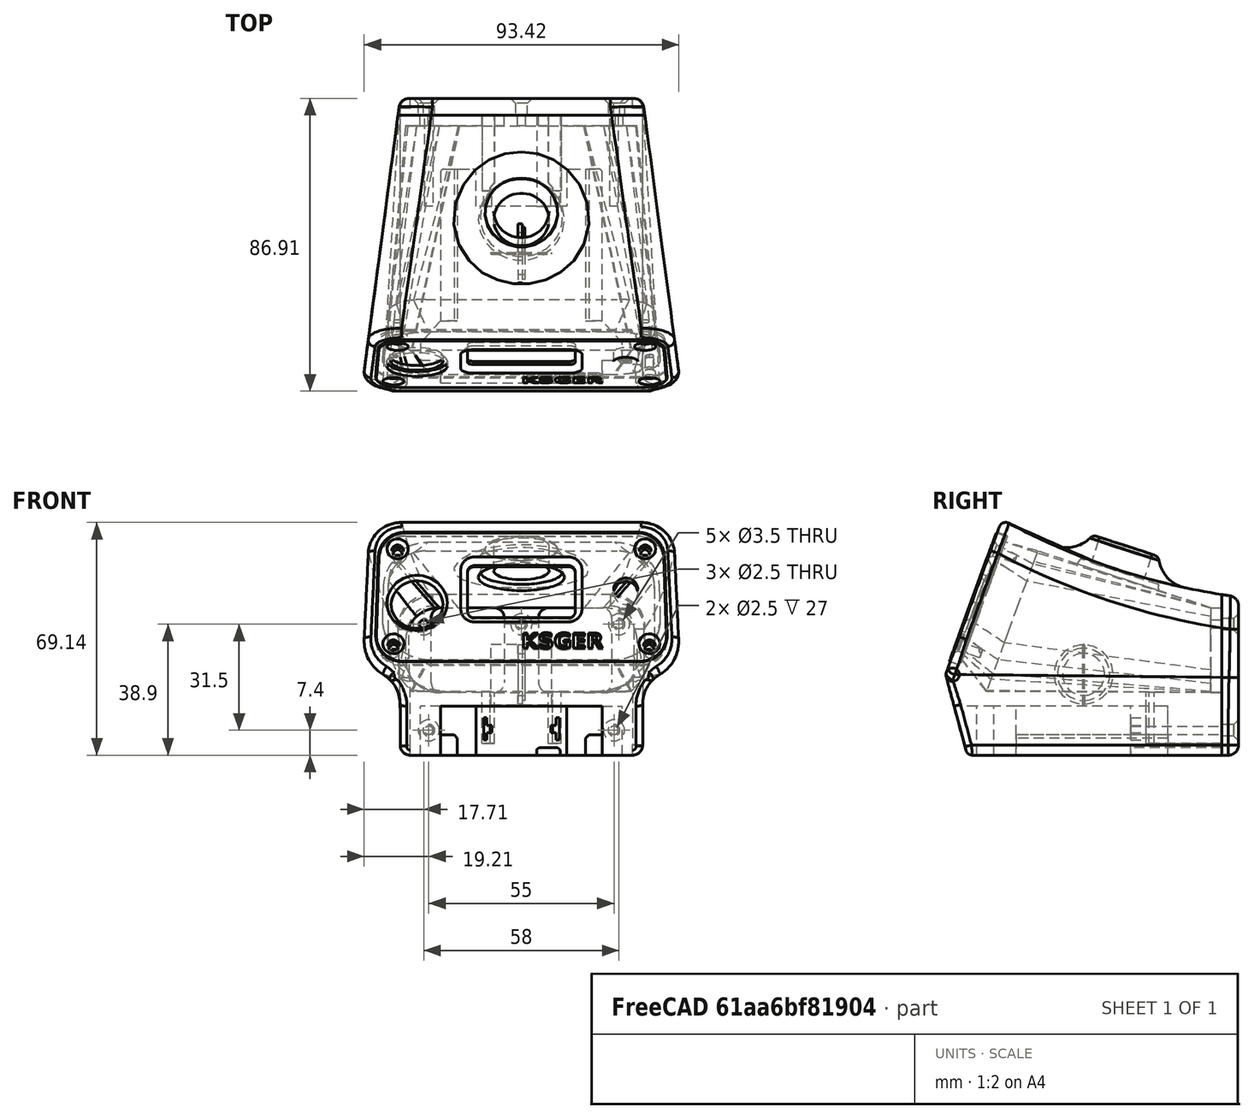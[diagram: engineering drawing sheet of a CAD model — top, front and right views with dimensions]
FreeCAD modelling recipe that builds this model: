
FCSTD DOCUMENT  (FreeCAD 2022.709R28846 (Git))
Label: solder_station5b_snap
License: All rights reserved
LicenseURL: http://en.wikipedia.org/wiki/All_rights_reserved
objects: Sketcher::SketchObject×22, PartDesign::Pocket×12, PartDesign::Fillet×8, Part::FeaturePython×6, Mesh::Feature×5, App::DocumentObjectGroup×4, PartDesign::Body×4, PartDesign::Chamfer×3, PartDesign::FeatureBase×2, PartDesign::Pad×2, PartDesign::Revolution×2, Spreadsheet::Sheet×1, Part::Plane×1, Part::Loft×1, Part::Extrusion×1, Part::MultiCommon×1, Part::Box×1, PartDesign::SubtractiveLoft×1, PartDesign::Groove×1, Part::Part2DObjectPython×1, +2 more types
note: 130 computed .brp shape members not serialized (recipe doc carries the construction recipe); baked Part::Feature solids carry a one-line shape summary decoded from their .brp

FEATURE [Sketcher::SketchObject] Sketch  label="RearSupport"
  ArcFitTolerance = 0
  AttachmentOffset = pos=(0,0,-37.8) rot=(0,0,1;0rad)
  AttachmentSupport = -> [XZ_Plane005]
  FullyConstrained = true
  MapMode = 5
  Placement = pos=(0,37.8,8.4e-15) rot=(1,0,0;1.5708rad)
  Support = -> [XZ_Plane005]
  TreeRank = 0
  expr: AttachmentOffset.Base.z = -<<param>>.mid_depth / 2 + <<param>>.wall
  expr: Constraints[24] = 3
  expr: Constraints[37] = <<param>>.bottom_height
  expr: Constraints[38] = <<param>>.floor
  expr: Constraints[39] = <<param>>.rear_height - <<param>>.wall
  expr: Constraints[47] = <<param>>.reart_screw_width2
  expr: Constraints[48] = <<param>>.rear_screw_width1
  expr: Constraints[49] = <<param>>.screw_hole
  expr: Constraints[50] = <<param>>.rear_screw_height
  expr: Constraints[51] = <<param>>.rear_screw_height
  expr: Constraints[52] = <<param>>.rear_screw_offset
  sketch-geometry (22):
    g0: LineSegment StartX=-23.8 StartY=19.8 StartZ=0 EndX=-8.1 EndY=19.8 EndZ=0
    g1: LineSegment StartX=26.8 StartY=16.8 StartZ=0 EndX=26.8 EndY=-2.4 EndZ=0
    g2: LineSegment StartX=23.8 StartY=-5.4 StartZ=0 EndX=8.1 EndY=-5.4 EndZ=0
    g3: LineSegment StartX=-26.8 StartY=-2.4 StartZ=0 EndX=-26.8 EndY=16.8 EndZ=0
    g4: LineSegment StartX=-5.1 StartY=16.8 StartZ=0 EndX=-5.1 EndY=-2.4 EndZ=0
    g5: LineSegment StartX=5.1 StartY=16.8 StartZ=0 EndX=5.1 EndY=-2.4 EndZ=0
    g6: LineSegment StartX=8.1 StartY=19.8 StartZ=0 EndX=23.8 EndY=19.8 EndZ=0
    g7: LineSegment StartX=-8.1 StartY=-5.4 StartZ=0 EndX=-23.8 EndY=-5.4 EndZ=0
    g8: ArcOfCircle CenterX=-8.1 CenterY=16.8 CenterZ=0 NormalX=0 NormalY=0 NormalZ=1 AngleXU=0 Radius=3 StartAngle=0 EndAngle=1.5708
    g9: ArcOfCircle CenterX=8.1 CenterY=16.8 CenterZ=0 NormalX=0 NormalY=0 NormalZ=1 AngleXU=0 Radius=3 StartAngle=1.5708 EndAngle=3.14159
    g10: ArcOfCircle CenterX=-8.1 CenterY=-2.4 CenterZ=0 NormalX=0 NormalY=0 NormalZ=1 AngleXU=0 Radius=3 StartAngle=4.71239 EndAngle=6.28319
    g11: ArcOfCircle CenterX=8.1 CenterY=-2.4 CenterZ=0 NormalX=0 NormalY=0 NormalZ=1 AngleXU=0 Radius=3 StartAngle=3.14159 EndAngle=4.71239
    g12: ArcOfCircle CenterX=-23.8 CenterY=16.8 CenterZ=0 NormalX=0 NormalY=0 NormalZ=1 AngleXU=0 Radius=3 StartAngle=1.5708 EndAngle=3.14159
    g13: ArcOfCircle CenterX=-23.8 CenterY=-2.4 CenterZ=0 NormalX=0 NormalY=0 NormalZ=1 AngleXU=0 Radius=3 StartAngle=3.14159 EndAngle=4.71239
    g14: ArcOfCircle CenterX=23.8 CenterY=16.8 CenterZ=0 NormalX=0 NormalY=0 NormalZ=1 AngleXU=0 Radius=3 StartAngle=3e-16 EndAngle=1.5708
    g15: ArcOfCircle CenterX=23.8 CenterY=-2.4 CenterZ=0 NormalX=0 NormalY=0 NormalZ=1 AngleXU=0 Radius=3 StartAngle=4.71239 EndAngle=6.28319
    g16: Circle [constr] CenterX=0 CenterY=-24 CenterZ=0 NormalX=0 NormalY=0 NormalZ=1 AngleXU=0 Radius=3
    g17: Circle CenterX=0 CenterY=14.9 CenterZ=0 NormalX=0 NormalY=0 NormalZ=1 AngleXU=0 Radius=1.25
    g18: Circle CenterX=-29 CenterY=14.9 CenterZ=0 NormalX=0 NormalY=0 NormalZ=1 AngleXU=0 Radius=1.25
    g19: Circle [constr] CenterX=-27.5 CenterY=-16.6 CenterZ=0 NormalX=0 NormalY=0 NormalZ=1 AngleXU=0 Radius=1.25
    g20: Circle [constr] CenterX=27.5 CenterY=-16.6 CenterZ=0 NormalX=0 NormalY=0 NormalZ=1 AngleXU=0 Radius=1.25
    g21: Circle CenterX=29 CenterY=14.9 CenterZ=0 NormalX=0 NormalY=0 NormalZ=1 AngleXU=0 Radius=1.25
  constraints (53):
    c: Horizontal(g0)
    c: Horizontal(g2)
    c: Vertical(g1)
    c: Vertical(g3)
    c: Vertical(g4)
    c: Vertical(g5)
    c: Tangent(g0,g6)
    c: Tangent(g2,g7)
    c: Tangent(g0,g8) = 1.5708
    c: Tangent(g4,g8) = 1.5708
    c: Tangent(g5,g9) = -1.5708
    c: Tangent(g6,g9) = 1.5708
    c: Tangent(g7,g10) = 1.5708
    c: Tangent(g4,g10) = 1.5708
    c: Tangent(g5,g11) = -1.5708
    c: Tangent(g2,g11) = 1.5708
    c: Tangent(g0,g12) = 1.5708
    c: Tangent(g3,g12) = 1.5708
    c: Tangent(g3,g13) = 1.5708
    c: Tangent(g7,g13) = 1.5708
    c: Tangent(g6,g14) = 1.5708
    c: Tangent(g1,g14) = 1.5708
    c: Tangent(g1,g15) = 1.5708
    c: Tangent(g2,g15) = 1.5708
    c: Radius(g9) = 3
    c: Equal(g12,g13)
    c: Equal(g13,g10)
    c: Equal(g10,g8)
    c: Equal(g11,g15)
    c: Equal(g15,g14)
    c: Equal(g14,g9)
    c: DistanceX(g4,g-1) = 5.1
    c: DistanceX(g5,g1) = 21.7
    c: Symmetric(g4,g5,g-2)
    c: Equal(g7,g2)
    c: PointOnObject(g16,g-2)
    c: Radius(g16) = 3
    c: DistanceY(g16,g-1) = 24
    c: DistanceY(g16,g2) = 18.6
    c: DistanceY(g16,g6) = 43.8
    c: PointOnObject(g17,g-2)
    c: Equal(g21,g18)
    c: Equal(g18,g19)
    c: Equal(g19,g20)
    c: Equal(g18,g17)
    c: Symmetric(g20,g19,g-2)
    c: Symmetric(g18,g21,g-2)
    c: DistanceX(g19,g20) = 55
    c: DistanceX(g18,g21) = 58
    c: Diameter(g19) = 2.5
    c: DistanceY(g20,g21) = 31.5
    c: DistanceY(g20,g17) = 31.5
    c: DistanceY(g16,g19) = 7.4
FEATURE [Spreadsheet::Sheet] Spreadsheet  label="param"
  PythonMode = false
  ShowCells = 0
  TreeRank = 0
  cells = A1=Body; B2=top_depth; C2(top_depth)=70; B3=mid_depth; C3(mid_depth)=82; D3=half is rear reference; B4=bottom_depth; C4(bottom_depth)=75; B6=bottom_width; C6(bottom_width)=72; B7=bottom_height; C7(bottom_height)=24; B8=bottom_angle; C8(bottom_angle)=15; B10=rear_width; C10(rear_width)=72; B11=rear_height; C11(rear_height)=47; F11=41; B13=mid_width; C13(mid_width)=80; B14=mid_height; C14(mid_height)=56; F14=50; B16=front_width1; C16(front_width1)=92; D16=@top; E16=upper; F16=91; B17=front_width2; C17(front_width2)=95; D17=@mid; E17=lower; F17=94; B18=front_height; C18(front_height)=70; F18=64; B19=front_angle; C19(front_angle)=20; B21=wall; C21(wall)=3.2; B22=radius_big; C22(radius_big)=10; B23=radius_medium; C23(radius_medium)=3; B24=radius_small; C24(radius_small)=2; B25=arch; C25(arch)=200; A27=Button; B28=button_offset; C28(button_offset)=10; B29=button_inside_dia; C29(button_inside_dia)=20; B30=button_outside_dia; C30(button_outside_dia)=22; B31=button_height; C31(button_height)=30.6; F31=26; B32=button_extension; C32(button_extension)=8; B33=button_fillet; C33(button_fillet)=12; B34=button_angle; C34(button_angle)=-18; F34=-17; B35=button_hole; C35(button_hole)=16.4; B36=button_hole_center; C36(button_hole_center)=-0.5; A38=Battery Cuts; B39=batt_carveout; C39(batt_carveout)=14.6; B40=batt_rail; C40(batt_rail)=6; B41=batt_rail_length; C41(batt_rail_length)=45; A43=Terminals; B44=terminal_height; C44(terminal_height)=6.6; B45=terminal_thickness; C45(terminal_thickness)=1; B46=terminal_seperation; C46(terminal_seperation)=21.5; B47=terminal_offset; C47(terminal_offset)=4.5; B48=terminal_depth; C48(terminal_depth)=22.5; A50=Box Interior; B51=floor; C51(floor)=18.6; B52=rear_inside_width; C52(rear_inside_width)==C10 - C21; D52=calc; B53=rear_inside_height; C53(rear_inside_height)==C11 - C21; D53=calc; B54=mid_inside_width; C54(mid_inside_width)==C13; D54=calc; B55=mid_inside_height; C55(mid_inside_height)==C14 + 7; D55=calc; F55=6; B56=front_inside_width1; C56(front_inside_width1)==C63 - C59 * 2; D56=calc; E56=upper; B57=front_inside_width2; C57(front_inside_width2)==C64 - C59 * 2; D57=calc; E57=lower; B58=front_inside_height; C58(front_inside_height)==C65 - C60 * 2; D58=calc; B59=front_width_lip_width; C59(front_width_lip_width)=3; B60=front_inside_lip_height; C60(front_inside_lip_height)=2; A62=Face; B63=face_width1; C63(face_width1)==84 + 1; B64=face_width2; C64(face_width2)==85.5 + 1; B65=face_height; C65(face_height)=41; F65=35; B66=face_thickness; C66(face_thickness)=3; B67=face_radius; C67(face_radius)=8; B68=face_offset; C68(face_offset)=2.8; F68=2.8; A70=Screws; B71=screw_hole; C71(screw_hole)=2.5; B73=front_screw_width1; C73(front_screw_width1)=73.5; D73=upper; B74=front_screw_width2; C74(front_screw_width2)=76; D74=lower; B75=front_screw_height; C75(front_screw_height)=30; F75=24; B76=front_screw_offset; C76(front_screw_offset)=5.5; B78=rear_screw_width1; C78(rear_screw_width1)=58; B79=reart_screw_width2; C79(reart_screw_width2)=55; B80=rear_screw_height; C80(rear_screw_height)=31.5; F80=25.5; B81=rear_screw_offset; C81(rear_screw_offset)=7.4; A83=Back; B84=back_thickness; C84(back_thickness)=5
FEATURE [Sketcher::SketchObject] Sketch008  label="SketchButtonHole"
  ArcFitTolerance = 0
  AttachmentOffset = pos=(0,-0.5,30.6) rot=(1,0,0;-0.314159rad)
  AttachmentSupport = -> [XY_Plane005]
  FullyConstrained = true
  MapMode = 5
  Placement = pos=(0,-0.5,30.6) rot=(1,0,0;5.96903rad)
  Support = -> [XY_Plane005]
  TreeRank = 0
  expr: AttachmentOffset.Base.y = <<param>>.button_hole_center
  expr: AttachmentOffset.Base.z = <<param>>.button_height
  expr: AttachmentOffset.Rotation.Angle = <<param>>.button_angle
  expr: Constraints[0] = <<param>>.button_hole
  expr: Constraints[2] = <<param>>.button_offset
  sketch-geometry (1):
    g0: Circle CenterX=0 CenterY=10 CenterZ=0 NormalX=0 NormalY=0 NormalZ=1 AngleXU=0 Radius=8.2
  constraints (3):
    c: Diameter(g0) = 16.4
    c: PointOnObject(g0,g-2)
    c: DistanceY(g-1,g0) = 10
FEATURE [Sketcher::SketchObject] Sketch012  label="SketchSide"
  ArcFitTolerance = 0
  AttachmentOffset = pos=(2.5,0,0) rot=(0,0,1;0rad)
  AttachmentSupport = -> [YZ_Plane006]
  FullyConstrained = true
  MapMode = 5
  Placement = pos=(6e-16,2.5,-6e-16) rot=(0.57735,0.57735,0.57735;2.0944rad)
  Support = -> [YZ_Plane006]
  TreeRank = 0
  expr: AttachmentOffset.Base.x = <<param>>.back_thickness / 2
  expr: Constraints[10] = <<param>>.bottom_height
  expr: Constraints[11] = 90 - <<param>>.bottom_angle
  expr: Constraints[12] = 90 - <<param>>.front_angle
  expr: Constraints[16] = <<param>>.front_height
  expr: Constraints[4] = <<param>>.rear_height - <<param>>.bottom_height
  expr: Constraints[5] = <<param>>.arch
  expr: Constraints[6] = <<param>>.mid_depth + <<param>>.back_thickness
  sketch-geometry (6):
    g0: LineSegment StartX=43.5 StartY=0 StartZ=0 EndX=43.5 EndY=23 EndZ=0
    g1: LineSegment StartX=-43.5 StartY=0 StartZ=0 EndX=-26.7574 EndY=46 EndZ=0
    g2: ArcOfCircle CenterX=69.5235 CenterY=221.3 CenterZ=0 NormalX=0 NormalY=0 NormalZ=1 AngleXU=0 Radius=200 StartAngle=4.21013 EndAngle=4.5819
    g3: LineSegment StartX=-43.5 StartY=0 StartZ=0 EndX=-37.0692 EndY=-24 EndZ=0
    g4: LineSegment StartX=-37.0692 StartY=-24 StartZ=0 EndX=43.5 EndY=-24 EndZ=0
    g5: LineSegment StartX=43.5 StartY=-24 StartZ=0 EndX=43.5 EndY=0 EndZ=0
  constraints (18):
    c: PointOnObject(g1,g-1)
    c: Vertical(g0)
    c: Coincident(g2,g0)
    c: Symmetric(g1,g0,g-2)
    c: DistanceY(g0,g0) = 23
    c: Radius(g2) = 200
    c: DistanceX(g1,g0) = 87
    c: Horizontal(g4)
    c: Coincident(g5,g4)
    c: Vertical(g5)
    c: DistanceY(g4,g-1) = 24
    c: Angle(g3,g-1) = 1.309
    c: Angle(g-1,g1) = 1.22173
    c: Coincident(g3,g1)
    c: Coincident(g5,g0)
    c: Coincident(g2,g1)
    c: DistanceY(g4,g1) = 70
    c: Coincident(g3,g4)
FEATURE [Sketcher::SketchObject] Sketch018  label="SketchBat1"
  ArcFitTolerance = 0
  AttachmentOffset = pos=(0,0,-24) rot=(0,0,1;0rad)
  AttachmentSupport = -> [XY_Plane005]
  FullyConstrained = true
  MapMode = 5
  Placement = pos=(0,0,-24) rot=(0,0,1;0rad)
  Support = -> [XY_Plane005]
  TreeRank = 0
  expr: AttachmentOffset.Base.z = -<<param>>.bottom_height
  expr: Constraints[63] = <<param>>.batt_rail_length
  expr: Constraints[64] = <<param>>.mid_depth / 2
  sketch-geometry (21):
    g0: LineSegment StartX=-24 StartY=-41.7082 StartZ=0 EndX=24 EndY=-41.7082 EndZ=0
    g1: LineSegment StartX=24 StartY=-41.7082 StartZ=0 EndX=24 EndY=-31.7082 EndZ=0
    g2: LineSegment StartX=24 StartY=-31.7082 StartZ=0 EndX=30 EndY=-31.7082 EndZ=0
    g3: LineSegment StartX=30 StartY=-31.7082 StartZ=0 EndX=30 EndY=-26.7082 EndZ=0
    g4: LineSegment StartX=30 StartY=-26.7082 StartZ=0 EndX=24 EndY=-20 EndZ=0
    g5: LineSegment StartX=24 StartY=-20 StartZ=0 EndX=24 EndY=24 EndZ=0
    g6: LineSegment StartX=13.5 StartY=24 StartZ=0 EndX=13.5 EndY=14 EndZ=0
    g7: LineSegment StartX=13.5 StartY=14 StartZ=0 EndX=-13.5 EndY=14 EndZ=0
    g8: LineSegment StartX=-13.5 StartY=14 StartZ=0 EndX=-13.5 EndY=24 EndZ=0
    g9: LineSegment StartX=-24 StartY=24 StartZ=0 EndX=-24 EndY=-20 EndZ=0
    g10: LineSegment StartX=-24 StartY=-20 StartZ=0 EndX=-30 EndY=-26.7082 EndZ=0
    g11: LineSegment StartX=-30 StartY=-26.7082 StartZ=0 EndX=-30 EndY=-31.7082 EndZ=0
    g12: LineSegment StartX=-30 StartY=-31.7082 StartZ=0 EndX=-24 EndY=-31.7082 EndZ=0
    g13: LineSegment StartX=-24 StartY=-31.7082 StartZ=0 EndX=-24 EndY=-41.7082 EndZ=0
    g14: Circle [constr] CenterX=0 CenterY=41 CenterZ=0 NormalX=0 NormalY=0 NormalZ=1 AngleXU=0 Radius=4
    g15: ArcOfCircle CenterX=-14.5 CenterY=24 CenterZ=0 NormalX=0 NormalY=0 NormalZ=1 AngleXU=0 Radius=1 StartAngle=6.28318 EndAngle=7.85399
    g16: LineSegment StartX=-23 StartY=25 StartZ=0 EndX=-14.5 EndY=25 EndZ=0
    g17: LineSegment StartX=14.5 StartY=25 StartZ=0 EndX=23 EndY=25 EndZ=0
    g18: ArcOfCircle CenterX=-23 CenterY=24 CenterZ=0 NormalX=0 NormalY=0 NormalZ=1 AngleXU=0 Radius=1 StartAngle=1.57079 EndAngle=3.1416
    g19: ArcOfCircle CenterX=14.5 CenterY=24 CenterZ=0 NormalX=0 NormalY=0 NormalZ=1 AngleXU=0 Radius=1 StartAngle=1.5708 EndAngle=3.14159
    g20: ArcOfCircle CenterX=23 CenterY=24 CenterZ=0 NormalX=0 NormalY=0 NormalZ=1 AngleXU=0 Radius=1.00001 StartAngle=2.75124e-06 EndAngle=1.5708
  constraints (65):
    c: Horizontal(g0)
    c: Coincident(g1,g0)
    c: Vertical(g1)
    c: Coincident(g2,g1)
    c: Horizontal(g2)
    c: Coincident(g3,g2)
    c: Coincident(g3,g4)
    c: Vertical(g5)
    c: Coincident(g6,g7)
    c: Coincident(g7,g8)
    c: Vertical(g8)
    c: Vertical(g9)
    c: Coincident(g10,g11)
    c: Vertical(g11)
    c: Coincident(g11,g12)
    c: Horizontal(g12)
    c: Coincident(g12,g13)
    c: Equal(g6,g8)
    c: Equal(g5,g9)
    c: Equal(g4,g10)
    c: Equal(g3,g11)
    c: Equal(g12,g2)
    c: Equal(g1,g13)
    c: Coincident(g13,g0)
    c: Vertical(g13)
    c: DistanceX(g7,g7) = 27
    c: Symmetric(g7,g6,g-2)
    c: Distance(g4) = 9
    c: Vertical(g3)
    c: DistanceY(g3,g3) = 5
    c: DistanceX(g2,g2) = 6
    c: DistanceY(g1,g1) = 10
    c: DistanceX(g0,g0) = 48
    c: PointOnObject(g14,g-2)
    c: Coincident(g9,g10)
    c: Coincident(g5,g4)
    c: Coincident(g15,g8)
    c: Coincident(g16,g15)
    c: Tangent(g15,g8)
    c: Horizontal(g16)
    c: Horizontal(g17)
    c: DistanceX(g9,g5) = 48
    c: Symmetric(g4,g9,g-2)
    c: Equal(g16,g17)
    c: Coincident(g18,g9)
    c: Coincident(g18,g16)
    c: Equal(g18,g15)
    c: Tangent(g18,g16)
    c: Tangent(g18,g9)
    c: DistanceY(g6,g17) = 11
    c: Vertical(g6)
    c: Coincident(g19,g6)
    c: Coincident(g19,g17)
    c: Coincident(g20,g17)
    c: Coincident(g20,g5)
    c: Tangent(g20,g17)
    c: Tangent(g20,g5)
    c: Tangent(g19,g6)
    c: Tangent(g19,g17)
    c: Equal(g15,g19)
    c: Radius(g19) = 1
    c: Radius(g14) = 4
    c: DistanceY(g15,g14) = 16
    c: DistanceY(g9,g16) = 45
    c: DistanceY(g-1,g14) = 41
FEATURE [Sketcher::SketchObject] Sketch019  label="SketchBat2"
  ArcFitTolerance = 0
  AttachmentOffset = pos=(0,0,-25) rot=(0,0,1;0rad)
  AttachmentSupport = -> [XZ_Plane005]
  FullyConstrained = true
  MapMode = 5
  Placement = pos=(0,25,5.6e-15) rot=(1,0,0;1.5708rad)
  Support = -> [XZ_Plane005]
  TreeRank = 0
  expr: AttachmentOffset.Base.z = -<<param>>.mid_depth / 2 + 16
  expr: Constraints[17] = <<param>>.bottom_height
  expr: Constraints[18] = <<param>>.batt_rail
  expr: Constraints[19] = 48.01mm
  sketch-geometry (10):
    g0: LineSegment StartX=-24.005 StartY=-18 StartZ=0 EndX=-20.005 EndY=-18 EndZ=0
    g1: LineSegment StartX=-19.005 StartY=-24 StartZ=0 EndX=-24.005 EndY=-24 EndZ=0
    g2: LineSegment StartX=-24.005 StartY=-24 StartZ=0 EndX=-24.005 EndY=-18 EndZ=0
    g3: LineSegment StartX=24.005 StartY=-18 StartZ=0 EndX=20.005 EndY=-18 EndZ=0
    g4: LineSegment StartX=19.005 StartY=-24 StartZ=0 EndX=24.005 EndY=-24 EndZ=0
    g5: LineSegment StartX=24.005 StartY=-24 StartZ=0 EndX=24.005 EndY=-18 EndZ=0
    g6: LineSegment StartX=-19.005 StartY=-19 StartZ=0 EndX=-19.005 EndY=-24 EndZ=0
    g7: LineSegment StartX=19.005 StartY=-24 StartZ=0 EndX=19.005 EndY=-19 EndZ=0
    g8: LineSegment StartX=-20.005 StartY=-18 StartZ=0 EndX=-19.005 EndY=-19 EndZ=0
    g9: LineSegment StartX=19.005 StartY=-19 StartZ=0 EndX=20.005 EndY=-18 EndZ=0
  constraints (29):
    c: Coincident(g1,g2)
    c: Coincident(g2,g0)
    c: Horizontal(g0)
    c: Horizontal(g1)
    c: Vertical(g2)
    c: Coincident(g4,g5)
    c: Coincident(g5,g3)
    c: Horizontal(g3)
    c: Horizontal(g4)
    c: Vertical(g5)
    c: Coincident(g6,g1)
    c: Vertical(g6)
    c: Equal(g1,g4)
    c: Coincident(g7,g4)
    c: Vertical(g7)
    c: Equal(g6,g7)
    c: Symmetric(g1,g4,g-2)
    c: DistanceY(g1,g-1) = 24
    c: DistanceY(g4,g3) = 6
    c: DistanceX(g1,g4) = 48.01
    c: DistanceX(g4,g4) = 5
    c: Coincident(g8,g0)
    c: Coincident(g8,g6)
    c: Coincident(g9,g7)
    c: Coincident(g9,g3)
    c: Equal(g0,g3)
    c: Equal(g2,g5)
    c: DistanceX(g0,g0) = 4
    c: DistanceY(g1,g6) = 5
FEATURE [Sketcher::SketchObject] Sketch021  label="SketchButton"
  ArcFitTolerance = 0
  AttachmentOffset = pos=(10,30.6,0) rot=(0,0,1;-0.314159rad)
  AttachmentSupport = -> [YZ_Plane005]
  FullyConstrained = true
  MapMode = 5
  Placement = pos=(-4.6e-15,10,30.6) rot=(-0.506732,-0.697457,-0.506732;4.35963rad)
  Support = -> [YZ_Plane005]
  TreeRank = 0
  expr: AttachmentOffset.Base.x = <<param>>.button_offset
  expr: AttachmentOffset.Base.y = <<param>>.button_height
  expr: AttachmentOffset.Rotation.Angle = <<param>>.button_angle
  expr: Constraints[6] = <<param>>.button_extension
  expr: Constraints[7] = <<param>>.button_outside_dia / 2
  sketch-geometry (5):
    g0: LineSegment StartX=0 StartY=0 StartZ=0 EndX=0 EndY=8 EndZ=0
    g1: LineSegment StartX=0 StartY=8 StartZ=0 EndX=9 EndY=8 EndZ=0
    g2: LineSegment StartX=0 StartY=0 StartZ=0 EndX=11 EndY=0 EndZ=0
    g3: LineSegment StartX=11 StartY=0 StartZ=0 EndX=11 EndY=6 EndZ=0
    g4: ArcOfCircle CenterX=9 CenterY=6 CenterZ=0 NormalX=0 NormalY=0 NormalZ=1 AngleXU=0 Radius=2 StartAngle=1e-16 EndAngle=1.5708
  constraints (13):
    c: Coincident(g0,g-1)
    c: PointOnObject(g0,g-2)
    c: Coincident(g1,g0)
    c: Horizontal(g1)
    c: Coincident(g2,g0)
    c: Horizontal(g2)
    c: DistanceY(g0,g0) = 8
    c: DistanceX(g2,g2) = 11
    c: Coincident(g3,g2)
    c: Vertical(g3)
    c: Radius(g4) = 2
    c: Tangent(g4,g1) = 1.5708
    c: Tangent(g4,g3) = -1.5708
FEATURE [Sketcher::SketchObject] Sketch022  label="SketchRearInside"
  ArcFitTolerance = 0
  AttachmentOffset = pos=(0,0,-37.8) rot=(0,0,1;0rad)
  AttachmentSupport = -> [XZ_Plane005]
  FullyConstrained = true
  MapMode = 5
  Placement = pos=(0,37.8,8.4e-15) rot=(1,0,0;1.5708rad)
  Support = -> [XZ_Plane005]
  TreeRank = 0
  expr: AttachmentOffset.Base.z = -<<param>>.mid_depth / 2 + <<param>>.wall
  expr: Constraints[12] = <<param>>.radius_big
  expr: Constraints[18] = <<param>>.rear_inside_width
  expr: Constraints[26] = <<param>>.bottom_height
  expr: Constraints[27] = <<param>>.rear_inside_height
  expr: Constraints[29] = <<param>>.floor
  sketch-geometry (9):
    g0: LineSegment StartX=-34.4 StartY=9.80003 StartZ=0 EndX=-34.4 EndY=4.59997 EndZ=0
    g1: LineSegment StartX=-24.4 StartY=-5.4 StartZ=0 EndX=24.4 EndY=-5.4 EndZ=0
    g2: LineSegment StartX=34.4 StartY=4.59997 StartZ=0 EndX=34.4 EndY=9.80003 EndZ=0
    g3: LineSegment StartX=-24.4 StartY=19.8 StartZ=0 EndX=24.4 EndY=19.8 EndZ=0
    g4: ArcOfCircle CenterX=24.4 CenterY=9.8 CenterZ=0 NormalX=0 NormalY=0 NormalZ=1 AngleXU=0 Radius=10 StartAngle=3.49027e-06 EndAngle=1.57079
    g5: ArcOfCircle CenterX=24.4 CenterY=4.6 CenterZ=0 NormalX=0 NormalY=0 NormalZ=1 AngleXU=0 Radius=10 StartAngle=4.71239 EndAngle=6.28318
    g6: ArcOfCircle CenterX=-24.4 CenterY=9.8 CenterZ=0 NormalX=0 NormalY=0 NormalZ=1 AngleXU=0 Radius=10 StartAngle=1.5708 EndAngle=3.14159
    g7: ArcOfCircle CenterX=-24.4 CenterY=4.6 CenterZ=0 NormalX=0 NormalY=0 NormalZ=1 AngleXU=0 Radius=10 StartAngle=3.1416 EndAngle=4.71239
    g8: Circle [constr] CenterX=0 CenterY=-24 CenterZ=0 NormalX=0 NormalY=0 NormalZ=1 AngleXU=0 Radius=3
  constraints (30):
    c: Vertical(g0)
    c: Horizontal(g1)
    c: Vertical(g2)
    c: Horizontal(g3)
    c: Equal(g3,g1)
    c: Equal(g0,g2)
    c: Coincident(g4,g3)
    c: Coincident(g4,g2)
    c: Coincident(g5,g2)
    c: Coincident(g5,g1)
    c: Coincident(g6,g0)
    c: Coincident(g6,g3)
    c: Radius(g6) = 10
    c: Equal(g6,g4)
    c: Equal(g4,g5)
    c: Coincident(g7,g1)
    c: Coincident(g7,g0)
    c: Equal(g5,g7)
    c: DistanceX(g0,g2) = 68.8
    c: Symmetric(g0,g2,g-2)
    c: Tangent(g4,g2)
    c: Tangent(g4,g3)
    c: Tangent(g5,g2)
    c: Tangent(g5,g1)
    c: Tangent(g6,g3)
    c: PointOnObject(g8,g-2)
    c: DistanceY(g8,g-1) = 24
    c: DistanceY(g8,g3) = 43.8
    c: Radius(g8) = 3
    c: DistanceY(g8,g1) = 18.6
FEATURE [Sketcher::SketchObject] Sketch024  label="SketchFaceCut"
  ArcFitTolerance = 0
  AttachmentOffset = pos=(0,0,37.6) rot=(1,0,0;-0.349066rad)
  AttachmentSupport = -> [XZ_Plane005]
  FullyConstrained = true
  MapMode = 5
  Placement = pos=(0,-37.6,-8.3e-15) rot=(-1,0,0;5.06145rad)
  Support = -> [XZ_Plane005]
  TreeRank = 0
  expr: AttachmentOffset.Base.z = <<param>>.mid_depth / 2 - <<param>>.face_thickness - 0.4
  expr: AttachmentOffset.Rotation.Angle = -<<param>>.front_angle
  expr: Constraints[13] = <<param>>.face_radius
  expr: Constraints[22] = <<param>>.face_width1
  expr: Constraints[23] = <<param>>.face_width2
  expr: Constraints[24] = <<param>>.face_offset
  expr: Constraints[25] = <<param>>.face_height
  sketch-geometry (8):
    g0: LineSegment StartX=-34.5035 StartY=43.8 StartZ=0 EndX=34.5037 EndY=43.8 EndZ=0
    g1: LineSegment StartX=42.5001 StartY=36.0399 StartZ=0 EndX=43.25 EndY=11.0399 EndZ=0
    g2: LineSegment StartX=35.2536 StartY=2.8 StartZ=0 EndX=-35.2536 EndY=2.8 EndZ=0
    g3: LineSegment StartX=-43.25 StartY=11.0399 StartZ=0 EndX=-42.4999 EndY=36.0399 EndZ=0
    g4: ArcOfCircle CenterX=34.5037 CenterY=35.8 CenterZ=0 NormalX=0 NormalY=0 NormalZ=1 AngleXU=0 Radius=8 StartAngle=0.0299879 EndAngle=1.5708
    g5: ArcOfCircle CenterX=35.2536 CenterY=10.8 CenterZ=0 NormalX=0 NormalY=0 NormalZ=1 AngleXU=0 Radius=8 StartAngle=4.71239 EndAngle=6.31317
    g6: ArcOfCircle CenterX=-34.5035 CenterY=35.8 CenterZ=0 NormalX=0 NormalY=0 NormalZ=1 AngleXU=0 Radius=8 StartAngle=1.5708 EndAngle=3.1116
    g7: ArcOfCircle CenterX=-35.2536 CenterY=10.8 CenterZ=0 NormalX=0 NormalY=0 NormalZ=1 AngleXU=0 Radius=8 StartAngle=3.1116 EndAngle=4.71239
  constraints (27):
    c: Horizontal(g0)
    c: Coincident(g4,g0)
    c: Coincident(g4,g1)
    c: Coincident(g5,g1)
    c: Coincident(g5,g2)
    c: Coincident(g6,g0)
    c: Coincident(g6,g3)
    c: Coincident(g7,g3)
    c: Coincident(g7,g2)
    c: Equal(g1,g3)
    c: Equal(g4,g6)
    c: Equal(g6,g7)
    c: Equal(g7,g5)
    c: Radius(g4) = 8
    c: Tangent(g6,g3)
    c: Tangent(g7,g3)
    c: Tangent(g7,g2)
    c: Tangent(g6,g0)
    c: Tangent(g4,g0)
    c: Tangent(g4,g1)
    c: Tangent(g5,g1)
    c: Tangent(g5,g2)
    c: DistanceX(g3,g1) = 85
    c: DistanceX(g3,g1) = 86.5
    c: DistanceY(g-1,g2) = 2.8
    c: DistanceY(g2,g0) = 41
    c: Symmetric(g2,g2,g-2)
FEATURE [Sketcher::SketchObject] Sketch025  label="SketchMidInside"
  ArcFitTolerance = 0
  AttachmentOffset = pos=(0,0,27) rot=(1,0,0;-0.349066rad)
  AttachmentSupport = -> [XZ_Plane005]
  FullyConstrained = true
  MapMode = 5
  Placement = pos=(0,-27,-6e-15) rot=(-1,0,0;5.06145rad)
  Support = -> [XZ_Plane005]
  TreeRank = 0
  expr: AttachmentOffset.Base.z = <<param>>.mid_depth / 2 - 14
  expr: AttachmentOffset.Rotation.Angle = -<<param>>.front_angle
  expr: Constraints[10] = <<param>>.radius_big + 1
  expr: Constraints[11] = <<param>>.floor
  expr: Constraints[12] = Spreadsheet.mid_inside_width - 1
  expr: Constraints[14] = <<param>>.mid_inside_height
  expr: Constraints[23] = <<param>>.mid_width - 15
  expr: Constraints[4] = <<param>>.bottom_height
  sketch-geometry (9):
    g0: LineSegment StartX=-28.5 StartY=39 StartZ=0 EndX=28.5 EndY=39 EndZ=0
    g1: LineSegment StartX=39.5 StartY=28 StartZ=0 EndX=39.5 EndY=10 EndZ=0
    g2: LineSegment StartX=32.5 StartY=-5.4 StartZ=0 EndX=-32.5 EndY=-5.4 EndZ=0
    g3: LineSegment StartX=-39.5 StartY=10 StartZ=0 EndX=-39.5 EndY=28 EndZ=0
    g4: Circle [constr] CenterX=0 CenterY=-24 CenterZ=0 NormalX=0 NormalY=0 NormalZ=1 AngleXU=0 Radius=3
    g5: ArcOfCircle CenterX=-28.5 CenterY=28 CenterZ=0 NormalX=0 NormalY=0 NormalZ=1 AngleXU=0 Radius=11 StartAngle=1.5708 EndAngle=3.14159
    g6: ArcOfCircle CenterX=28.5 CenterY=28 CenterZ=0 NormalX=0 NormalY=0 NormalZ=1 AngleXU=0 Radius=11 StartAngle=0 EndAngle=1.5708
    g7: ArcOfCircle CenterX=-15.553 CenterY=11.5941 CenterZ=0 NormalX=0 NormalY=0 NormalZ=1 AngleXU=0 Radius=24 StartAngle=3.20806 EndAngle=3.92838
    g8: ArcOfCircle CenterX=15.553 CenterY=11.5941 CenterZ=0 NormalX=0 NormalY=0 NormalZ=1 AngleXU=0 Radius=24 StartAngle=5.4964 EndAngle=6.21672
  constraints (25):
    c: Vertical(g1)
    c: Vertical(g3)
    c: PointOnObject(g4,g-2)
    c: Radius(g4) = 3
    c: DistanceY(g4,g-1) = 24
    c: Tangent(g3,g5) = 1.5708
    c: Tangent(g0,g5) = 1.5708
    c: Tangent(g0,g6) = 1.5708
    c: Tangent(g1,g6) = 1.5708
    c: Equal(g6,g5)
    c: Radius(g6) = 11
    c: DistanceY(g4,g2) = 18.6
    c: DistanceX(g3,g1) = 79
    c: Symmetric(g2,g2,g-2)
    c: DistanceY(g4,g0) = 63
    c: Symmetric(g0,g0,g-2)
    c: Equal(g3,g1)
    c: Coincident(g7,g2)
    c: Coincident(g8,g1)
    c: Coincident(g8,g2)
    c: Coincident(g7,g3)
    c: Equal(g8,g7)
    c: Radius(g8) = 24
    c: DistanceX(g2,g2) = 65
    c: DistanceY(g1,g1) = 18
FEATURE [Sketcher::SketchObject] Sketch026  label="SketchFrontScrews"
  ArcFitTolerance = 0
  AttachmentOffset = pos=(0,0,38) rot=(1,0,0;-0.349066rad)
  AttachmentSupport = -> [XZ_Plane005]
  FullyConstrained = true
  MapMode = 5
  Placement = pos=(0,-38,-8.4e-15) rot=(-1,0,0;5.06145rad)
  Support = -> [XZ_Plane005]
  TreeRank = 0
  expr: AttachmentOffset.Base.z = <<param>>.mid_depth / 2 - <<param>>.face_thickness
  expr: AttachmentOffset.Rotation.Angle = -<<param>>.front_angle
  expr: Constraints[0] = <<param>>.front_screw_width1
  expr: Constraints[13] = <<param>>.screw_hole
  expr: Constraints[1] = <<param>>.front_screw_width2
  expr: Constraints[2] = <<param>>.front_screw_height
  expr: Constraints[9] = <<param>>.face_offset + <<param>>.front_screw_offset
  sketch-geometry (6):
    g0: Circle CenterX=-36.75 CenterY=38.3 CenterZ=0 NormalX=0 NormalY=0 NormalZ=1 AngleXU=0 Radius=1.25
    g1: Circle CenterX=36.75 CenterY=38.3 CenterZ=0 NormalX=0 NormalY=0 NormalZ=1 AngleXU=0 Radius=1.25
    g2: Circle CenterX=-38 CenterY=8.3 CenterZ=0 NormalX=0 NormalY=0 NormalZ=1 AngleXU=0 Radius=1.25
    g3: Circle CenterX=38 CenterY=8.3 CenterZ=0 NormalX=0 NormalY=0 NormalZ=1 AngleXU=0 Radius=1.25
    g4: LineSegment [constr] StartX=-36.75 StartY=38.3 StartZ=0 EndX=36.75 EndY=38.3 EndZ=0
    g5: LineSegment [constr] StartX=-38 StartY=8.3 StartZ=0 EndX=38 EndY=8.3 EndZ=0
  constraints (14):
    c: DistanceX(g0,g1) = 73.5
    c: DistanceX(g2,g3) = 76
    c: DistanceY(g3,g1) = 30
    c: Coincident(g4,g0)
    c: Coincident(g4,g1)
    c: Coincident(g5,g2)
    c: Coincident(g5,g3)
    c: Symmetric(g2,g3,g-2)
    c: Symmetric(g0,g1,g-2)
    c: DistanceY(g-1,g3) = 8.3
    c: Equal(g0,g2)
    c: Equal(g2,g3)
    c: Equal(g3,g1)
    c: Diameter(g0) = 2.5
FEATURE [Sketcher::SketchObject] Sketch023  label="SketchFrontInside"
  ArcFitTolerance = 0
  AttachmentOffset = pos=(0,0,38) rot=(1,0,0;-0.349066rad)
  AttachmentSupport = -> [XZ_Plane005]
  ExternalGeometry = -> [Sketch026,Sketch024]
  FullyConstrained = true
  MapMode = 5
  Placement = pos=(0,-38,-8.4e-15) rot=(-1,0,0;5.06145rad)
  Support = -> [XZ_Plane005]
  TreeRank = 0
  expr: AttachmentOffset.Base.z = <<param>>.mid_depth / 2 - <<param>>.face_thickness
  expr: AttachmentOffset.Rotation.Angle = -<<param>>.front_angle
  sketch-geometry (16):
    g0: LineSegment StartX=-27.5 StartY=4.93681 StartZ=0 EndX=27.5 EndY=4.93681 EndZ=0
    g1: LineSegment StartX=27.5 StartY=41.9368 StartZ=0 EndX=-27.5 EndY=41.9368 EndZ=0
    g2: LineSegment StartX=-40.95 StartY=28.0001 StartZ=0 EndX=-41.25 EndY=18.0001 EndZ=0
    g3: LineSegment StartX=40.95 StartY=28 StartZ=0 EndX=41.25 EndY=18 EndZ=0
    g4: ArcOfCircle CenterX=36.75 CenterY=38.3 CenterZ=0 NormalX=0 NormalY=0 NormalZ=1 AngleXU=0 Radius=3 StartAngle=2.46996 EndAngle=5.23357
    g5: ArcOfCircle CenterX=27.5 CenterY=27.5965 CenterZ=0 NormalX=0 NormalY=0 NormalZ=1 AngleXU=0 Radius=13.4561 StartAngle=0.0299886 EndAngle=0.646116
    g6: ArcOfCircle CenterX=27.5 CenterY=27.5965 CenterZ=0 NormalX=0 NormalY=0 NormalZ=1 AngleXU=0 Radius=14.3403 StartAngle=1.06869 EndAngle=1.5708
    g7: ArcOfCircle CenterX=38 CenterY=8.3 CenterZ=0 NormalX=0 NormalY=0 NormalZ=1 AngleXU=0 Radius=3 StartAngle=1.04133 EndAngle=3.41706
    g8: ArcOfCircle CenterX=27.5 CenterY=17.5875 CenterZ=0 NormalX=0 NormalY=0 NormalZ=1 AngleXU=0 Radius=13.7562 StartAngle=5.77461 EndAngle=6.31317
    g9: ArcOfCircle CenterX=27.5 CenterY=17.5875 CenterZ=0 NormalX=0 NormalY=0 NormalZ=1 AngleXU=0 Radius=12.6507 StartAngle=4.71239 EndAngle=5.35813
    g10: ArcOfCircle CenterX=-36.75 CenterY=38.3 CenterZ=0 NormalX=0 NormalY=0 NormalZ=1 AngleXU=0 Radius=3 StartAngle=4.19123 EndAngle=6.95482
    g11: ArcOfCircle CenterX=-27.5 CenterY=27.5965 CenterZ=0 NormalX=0 NormalY=0 NormalZ=1 AngleXU=0 Radius=13.456 StartAngle=2.49548 EndAngle=3.1116
    g12: ArcOfCircle CenterX=-27.5 CenterY=27.5965 CenterZ=0 NormalX=0 NormalY=0 NormalZ=1 AngleXU=0 Radius=14.3403 StartAngle=1.5708 EndAngle=2.0729
    g13: ArcOfCircle CenterX=-38 CenterY=8.3 CenterZ=0 NormalX=0 NormalY=0 NormalZ=1 AngleXU=0 Radius=3 StartAngle=6.00771 EndAngle=8.38345
    g14: ArcOfCircle CenterX=-27.5 CenterY=17.5875 CenterZ=0 NormalX=0 NormalY=0 NormalZ=1 AngleXU=0 Radius=13.7562 StartAngle=3.1116 EndAngle=3.65016
    g15: ArcOfCircle CenterX=-27.5 CenterY=17.5875 CenterZ=0 NormalX=0 NormalY=0 NormalZ=1 AngleXU=0 Radius=12.6507 StartAngle=4.06665 EndAngle=4.71239
  constraints (42):
    c: Symmetric(g0,g0,g-2)
    c: Symmetric(g1,g1,g-2)
    c: DistanceY(g3,g3) = 10
    c: Equal(g3,g2)
    c: Equal(g1,g0)
    c: DistanceX(g1,g1) = 55
    c: Coincident(g4,g-3)
    c: Coincident(g5,g4)
    c: Coincident(g6,g4)
    c: Radius(g4) = 3
    c: Tangent(g5,g3) = 1.5708
    c: Parallel(g3,g-8)
    c: Tangent(g6,g1) = -1.5708
    c: DistanceX(g3,g-8) = 2
    c: Parallel(g-7,g2)
    c: DistanceX(g-7,g2) = 2
    c: Coincident(g7,g-4)
    c: Coincident(g8,g7)
    c: Coincident(g9,g7)
    c: Tangent(g8,g3) = 1.5708
    c: Tangent(g9,g0) = -1.5708
    c: Coincident(g9,g8)
    c: Coincident(g5,g6)
    c: DistanceY(g-10,g0) = 2
    c: DistanceY(g1,g-9) = 2
    c: Coincident(g10,g-6)
    c: Coincident(g11,g10)
    c: Coincident(g12,g10)
    c: Coincident(g13,g-5)
    c: Coincident(g14,g13)
    c: Coincident(g15,g13)
    c: Tangent(g12,g1) = -1.5708
    c: Tangent(g11,g2) = -1.5708
    c: Coincident(g11,g12)
    c: Coincident(g14,g15)
    c: Tangent(g14,g2) = -1.5708
    c: Tangent(g15,g0) = -1.5708
    c: Equal(g10,g13)
    c: Equal(g13,g7)
    c: Equal(g7,g4)
    c: Equal(g12,g6)
    c: DistanceY(g-1,g3) = 18
FEATURE [Sketcher::SketchObject] Sketch027  label="SketchButtonCarve"
  ArcFitTolerance = 0
  AttachmentOffset = pos=(10,28.6,0) rot=(0,0,1;-0.314159rad)
  AttachmentSupport = -> [YZ_Plane005]
  FullyConstrained = true
  MapMode = 5
  Placement = pos=(-4.1e-15,10,28.6) rot=(-0.506732,-0.697457,-0.506732;4.35963rad)
  Support = -> [YZ_Plane005]
  TreeRank = 0
  expr: AttachmentOffset.Base.x = <<param>>.button_offset
  expr: AttachmentOffset.Base.y = <<param>>.button_height - 2
  expr: AttachmentOffset.Rotation.Angle = <<param>>.button_angle
  expr: Constraints[12] = <<param>>.button_hole / 2 + 10
  expr: Constraints[6] = <<param>>.button_hole / 2 + 4
  sketch-geometry (4):
    g0: LineSegment StartX=0 StartY=2 StartZ=0 EndX=12.2 EndY=2 EndZ=0
    g1: ArcOfCircle CenterX=18.2 CenterY=3.09999 CenterZ=0 NormalX=0 NormalY=0 NormalZ=1 AngleXU=0 Radius=6.09999 StartAngle=3.32291 EndAngle=4.71239
    g2: LineSegment StartX=0 StartY=2 StartZ=0 EndX=0 EndY=-3 EndZ=0
    g3: LineSegment StartX=18.2 StartY=-3 StartZ=0 EndX=0 EndY=-3 EndZ=0
  constraints (13):
    c: Horizontal(g0)
    c: Coincident(g1,g0)
    c: Coincident(g2,g0)
    c: Coincident(g3,g1)
    c: Horizontal(g3)
    c: Tangent(g3,g1)
    c: DistanceX(g0,g0) = 12.2
    c: DistanceY(g2,g2) = 5
    c: Coincident(g2,g3)
    c: Vertical(g2)
    c: PointOnObject(g-1,g2)
    c: DistanceY(g2,g-1) = 3
    c: DistanceX(g3,g3) = 18.2
FEATURE [Sketcher::SketchObject] Sketch028  label="SketchTerminals"
  ArcFitTolerance = 0
  AttachmentSupport = -> [XZ_Plane005]
  FullyConstrained = true
  MapMode = 5
  Placement = pos=(0,0,0) rot=(1,0,0;1.5708rad)
  Support = -> [XZ_Plane005]
  TreeRank = 0
  expr: Constraints[17] = <<param>>.terminal_thickness
  expr: Constraints[18] = <<param>>.terminal_height
  expr: Constraints[21] = <<param>>.bottom_height
  expr: Constraints[22] = <<param>>.terminal_offset
  expr: Constraints[23] = <<param>>.terminal_seperation
  sketch-geometry (17):
    g0: LineSegment StartX=10.25 StartY=-12.9 StartZ=0 EndX=11.25 EndY=-12.9 EndZ=0
    g1: LineSegment StartX=11.25 StartY=-12.9 StartZ=0 EndX=11.25 EndY=-19.5 EndZ=0
    g2: LineSegment StartX=11.25 StartY=-19.5 StartZ=0 EndX=10.25 EndY=-19.5 EndZ=0
    g3: LineSegment StartX=10.25 StartY=-19.5 StartZ=0 EndX=10.25 EndY=-17.25 EndZ=0
    g4: LineSegment StartX=-10.25 StartY=-12.9 StartZ=0 EndX=-11.25 EndY=-12.9 EndZ=0
    g5: LineSegment StartX=-11.25 StartY=-12.9 StartZ=0 EndX=-11.25 EndY=-19.5 EndZ=0
    g6: LineSegment StartX=-11.25 StartY=-19.5 StartZ=0 EndX=-10.25 EndY=-19.5 EndZ=0
    g7: LineSegment StartX=-10.25 StartY=-19.5 StartZ=0 EndX=-10.25 EndY=-17.25 EndZ=0
    g8: Circle [constr] CenterX=0 CenterY=-24 CenterZ=0 NormalX=0 NormalY=0 NormalZ=1 AngleXU=0 Radius=3
    g9: LineSegment StartX=-10.25 StartY=-15.15 StartZ=0 EndX=-8.75 EndY=-15.15 EndZ=0
    g10: LineSegment StartX=-8.75 StartY=-15.15 StartZ=0 EndX=-8.75 EndY=-17.25 EndZ=0
    g11: LineSegment StartX=-8.75 StartY=-17.25 StartZ=0 EndX=-10.25 EndY=-17.25 EndZ=0
    g12: LineSegment StartX=-10.25 StartY=-15.15 StartZ=0 EndX=-10.25 EndY=-12.9 EndZ=0
    g13: LineSegment StartX=10.25 StartY=-15.15 StartZ=0 EndX=8.75 EndY=-15.15 EndZ=0
    g14: LineSegment StartX=8.75 StartY=-15.15 StartZ=0 EndX=8.75 EndY=-17.25 EndZ=0
    g15: LineSegment StartX=8.75 StartY=-17.25 StartZ=0 EndX=10.25 EndY=-17.25 EndZ=0
    g16: LineSegment StartX=10.25 StartY=-15.15 StartZ=0 EndX=10.25 EndY=-12.9 EndZ=0
  constraints (48):
    c: Coincident(g0,g1)
    c: Coincident(g1,g2)
    c: Coincident(g2,g3)
    c: Coincident(g16,g0)
    c: Horizontal(g0)
    c: Horizontal(g2)
    c: Vertical(g1)
    c: Vertical(g3)
    c: Coincident(g4,g5)
    c: Coincident(g5,g6)
    c: Coincident(g6,g7)
    c: Coincident(g12,g4)
    c: Horizontal(g4)
    c: Horizontal(g6)
    c: Vertical(g5)
    c: Vertical(g7)
    c: Equal(g4,g0)
    c: DistanceX(g4,g4) = 1
    c: DistanceY(g3,g16) = 6.6
    c: PointOnObject(g8,g-2)
    c: Radius(g8) = 3
    c: DistanceY(g8,g-1) = 24
    c: DistanceY(g8,g1) = 4.5
    c: DistanceX(g6,g1) = 21.5
    c: Symmetric(g4,g0,g-2)
    c: Horizontal(g9)
    c: Coincident(g10,g9)
    c: Vertical(g10)
    c: Coincident(g11,g10)
    c: Horizontal(g11)
    c: Coincident(g7,g11)
    c: Coincident(g12,g9)
    c: Tangent(g7,g12)
    c: Equal(g12,g7)
    c: Horizontal(g5,g1)
    c: DistanceY(g10,g10) = 2.1
    c: DistanceX(g9,g9) = 1.5
    c: Horizontal(g13)
    c: Coincident(g14,g13)
    c: Vertical(g14)
    c: Coincident(g15,g14)
    c: Horizontal(g15)
    c: Coincident(g3,g15)
    c: Coincident(g16,g13)
    c: Tangent(g3,g16)
    c: Equal(g16,g3)
    c: Equal(g13,g9)
    c: Equal(g14,g10)
FEATURE [Sketcher::SketchObject] Sketch029  label="SketchAccess"
  ArcFitTolerance = 0
  AttachmentOffset = pos=(0,0,-20.5) rot=(0,0,1;0rad)
  AttachmentSupport = -> [XY_Plane005]
  FullyConstrained = true
  MapMode = 5
  Placement = pos=(0,0,-20.5) rot=(0,0,1;0rad)
  Support = -> [XY_Plane005]
  TreeRank = 0
  expr: AttachmentOffset.Base.z = -<<param>>.bottom_height + <<param>>.terminal_offset - 1
  expr: Constraints[19] = <<param>>.mid_depth / 2
  expr: Constraints[22] = <<param>>.terminal_seperation + <<param>>.terminal_thickness * 2
  expr: Constraints[23] = <<param>>.terminal_depth
  sketch-geometry (12):
    g0: LineSegment StartX=-11.75 StartY=41 StartZ=0 EndX=-11.75 EndY=18.5 EndZ=0
    g1: LineSegment StartX=-11.75 StartY=18.5 StartZ=0 EndX=-9.25 EndY=18.5 EndZ=0
    g2: LineSegment StartX=-7.95 StartY=21 StartZ=0 EndX=-7.95 EndY=41 EndZ=0
    g3: LineSegment StartX=-7.95 StartY=41 StartZ=0 EndX=-11.75 EndY=41 EndZ=0
    g4: LineSegment StartX=7.95 StartY=41 StartZ=0 EndX=11.75 EndY=41 EndZ=0
    g5: LineSegment StartX=11.75 StartY=41 StartZ=0 EndX=11.75 EndY=18.5 EndZ=0
    g6: LineSegment StartX=11.75 StartY=18.5 StartZ=0 EndX=9.25 EndY=18.5 EndZ=0
    g7: LineSegment StartX=7.95 StartY=21 StartZ=0 EndX=7.95 EndY=41 EndZ=0
    g8: LineSegment StartX=9.25 StartY=18.5 StartZ=0 EndX=9.25 EndY=19.5 EndZ=0
    g9: LineSegment StartX=7.95 StartY=21 StartZ=0 EndX=9.25 EndY=19.5 EndZ=0
    g10: LineSegment StartX=-9.25 StartY=18.5 StartZ=0 EndX=-9.25 EndY=19.5 EndZ=0
    g11: LineSegment StartX=-9.25 StartY=19.5 StartZ=0 EndX=-7.95 EndY=21 EndZ=0
  constraints (35):
    c: Vertical(g0)
    c: Coincident(g0,g1)
    c: Vertical(g2)
    c: Coincident(g2,g3)
    c: Coincident(g3,g0)
    c: Horizontal(g3)
    c: Horizontal(g4)
    c: Coincident(g4,g5)
    c: Vertical(g5)
    c: Coincident(g5,g6)
    c: Horizontal(g6)
    c: Coincident(g7,g4)
    c: Vertical(g7)
    c: Equal(g3,g4)
    c: Equal(g0,g5)
    c: Horizontal(g1)
    c: Equal(g2,g7)
    c: Equal(g1,g6)
    c: Symmetric(g2,g4,g-2)
    c: DistanceY(g-1,g0) = 41
    c: DistanceX(g1,g1) = 2.5
    c: DistanceX(g0,g2) = 3.8
    c: DistanceX(g0,g5) = 23.5
    c: DistanceY(g5,g4) = 22.5
    c: DistanceY(g2,g2) = 20
    c: Coincident(g8,g6) = 23.5
    c: Vertical(g8) = 22
    c: Coincident(g9,g7)
    c: Coincident(g9,g8)
    c: Coincident(g10,g1)
    c: Coincident(g11,g10)
    c: Coincident(g11,g2)
    c: Equal(g8,g10)
    c: DistanceY(g8,g8) = 1
    c: Vertical(g10)
FEATURE [Sketcher::SketchObject] Sketch030  label="SketchFront"
  ArcFitTolerance = 0
  AttachmentOffset = pos=(0,0,41) rot=(0,0,1;0rad)
  AttachmentSupport = -> [XZ_Plane006]
  FullyConstrained = true
  MapMode = 5
  Placement = pos=(0,-41,-9.1e-15) rot=(1,0,0;1.5708rad)
  Support = -> [XZ_Plane006]
  TreeRank = 0
  expr: AttachmentOffset.Base.z = <<param>>.mid_depth / 2
  expr: Constraints[16] = <<param>>.radius_big * 1.2
  expr: Constraints[21] = <<param>>.radius_big
  expr: Constraints[2] = <<param>>.bottom_width
  expr: Constraints[4] = <<param>>.bottom_height + 10
  expr: Constraints[5] = <<param>>.front_width2
  expr: Constraints[6] = <<param>>.front_width2
  expr: Constraints[7] = <<param>>.front_height + 20
  sketch-geometry (10):
    g0: LineSegment StartX=-47.5 StartY=56 StartZ=0 EndX=47.5 EndY=56 EndZ=0
    g1: LineSegment StartX=47.5 StartY=56 StartZ=0 EndX=47.5 EndY=10.5451 EndZ=0
    g2: LineSegment StartX=36 StartY=-8.78755 StartZ=0 EndX=36 EndY=-34 EndZ=0
    g3: LineSegment StartX=36 StartY=-34 StartZ=0 EndX=-36 EndY=-34 EndZ=0
    g4: LineSegment StartX=-36 StartY=-34 StartZ=0 EndX=-36 EndY=-8.78755 EndZ=0
    g5: LineSegment StartX=-47.5 StartY=10.5451 StartZ=0 EndX=-47.5 EndY=56 EndZ=0
    g6: ArcOfCircle CenterX=46 CenterY=-8.78755 CenterZ=0 NormalX=0 NormalY=0 NormalZ=1 AngleXU=0 Radius=10 StartAngle=2.06834 EndAngle=3.14159
    g7: ArcOfCircle CenterX=35.5 CenterY=10.5451 CenterZ=0 NormalX=0 NormalY=0 NormalZ=1 AngleXU=0 Radius=12 StartAngle=5.20994 EndAngle=6.28319
    g8: ArcOfCircle CenterX=-46 CenterY=-8.78755 CenterZ=0 NormalX=0 NormalY=0 NormalZ=1 AngleXU=0 Radius=10 StartAngle=1e-16 EndAngle=1.07325
    g9: ArcOfCircle CenterX=-35.5 CenterY=10.5451 CenterZ=0 NormalX=0 NormalY=0 NormalZ=1 AngleXU=0 Radius=12 StartAngle=3.14159 EndAngle=4.21484
  constraints (26):
    c: Vertical(g2)
    c: Vertical(g4)
    c: DistanceX(g4,g2) = 72
    c: Symmetric(g3,g3,g-2)
    c: DistanceY(g3,g-1) = 34
    c: DistanceX(g5,g1) = 95
    c: DistanceX(g5,g1) = 95
    c: DistanceY(g3,g0) = 90
    c: Equal(g8,g6)
    c: Symmetric(g5,g1,g-2)
    c: Equal(g4,g2)
    c: Coincident(g6,g2)
    c: Coincident(g0,g1)
    c: Coincident(g5,g0)
    c: Symmetric(g0,g0,g-2)
    c: Equal(g7,g9)
    c: Radius(g7) = 12
    c: Tangent(g9,g5) = 1.5708
    c: Tangent(g1,g7) = 1.5708
    c: Tangent(g9,g8) = 1.5708
    c: Tangent(g6,g7) = 1.5708
    c: Radius(g6) = 10
    c: DistanceY(g6,g-1) = 0
    c: Tangent(g8,g4) = -1.5708
    c: Coincident(g3,g2)
    c: Coincident(g3,g4)
FEATURE [Sketcher::SketchObject] Sketch031  label="SketchRear"
  ArcFitTolerance = 0
  AttachmentOffset = pos=(0,0,-46) rot=(0,0,1;0rad)
  AttachmentSupport = -> [XZ_Plane006]
  FullyConstrained = true
  MapMode = 5
  Placement = pos=(0,46,1.02e-14) rot=(1,0,0;1.5708rad)
  Support = -> [XZ_Plane006]
  TreeRank = 0
  expr: AttachmentOffset.Base.z = -<<param>>.mid_depth / 2 - <<param>>.back_thickness
  expr: Constraints[1] = <<param>>.bottom_height + 10
  expr: Constraints[2] = <<param>>.rear_width
  expr: Constraints[6] = <<param>>.front_height + 20
  sketch-geometry (4):
    g0: LineSegment StartX=-36 StartY=-34 StartZ=0 EndX=36 EndY=-34 EndZ=0
    g1: LineSegment StartX=36 StartY=56 StartZ=0 EndX=-36 EndY=56 EndZ=0
    g2: LineSegment StartX=36 StartY=-34 StartZ=0 EndX=36 EndY=56 EndZ=0
    g3: LineSegment StartX=-36 StartY=-34 StartZ=0 EndX=-36 EndY=56 EndZ=0
  constraints (12):
    c: Horizontal(g0)
    c: DistanceY(g0,g-1) = 34
    c: DistanceX(g3,g2) = 72
    c: Vertical(g2)
    c: Equal(g3,g2)
    c: Vertical(g3)
    c: DistanceY(g0,g1) = 90
    c: Symmetric(g2,g3,g-2)
    c: Coincident(g2,g1)
    c: Coincident(g3,g1)
    c: Coincident(g2,g0)
    c: Equal(g1,g0)
FEATURE [Part::Plane] Plane002  label="PlaneDivider"
  AttacherType = Attacher::AttachEngine3D
  AttachmentSupport = -> [XZ_Plane006]
  Length = 152
  Placement = pos=(-75,41,-75) rot=(1,0,0;1.5708rad)
  Support = -> [XZ_Plane006]
  TreeRank = 0
  Width = 150
  expr: Placement.Base.y = <<param>>.mid_depth / 2
FEATURE [Sketcher::SketchObject] Sketch032  label="SketchBack"
  ArcFitTolerance = 0
  AttachmentSupport = -> [XZ_Plane]
  FullyConstrained = true
  MapMode = 5
  Placement = pos=(0,0,0) rot=(1,0,0;1.5708rad)
  Support = -> [XZ_Plane]
  TreeRank = 0
  expr: Constraints[10] = <<param>>.rear_screw_width1
  expr: Constraints[11] = <<param>>.reart_screw_width2
  expr: Constraints[12] = <<param>>.rear_screw_height
  expr: Constraints[15] = <<param>>.rear_screw_offset
  expr: Constraints[1] = <<param>>.bottom_height
  expr: Constraints[2] = <<param>>.rear_width
  expr: Constraints[9] = <<param>>.screw_hole + 1
  sketch-geometry (6):
    g0: LineSegment [constr] StartX=36 StartY=-24 StartZ=0 EndX=-36 EndY=-24 EndZ=0
    g1: Circle CenterX=-29 CenterY=14.9 CenterZ=0 NormalX=0 NormalY=0 NormalZ=1 AngleXU=0 Radius=1.75
    g2: Circle CenterX=0 CenterY=14.9 CenterZ=0 NormalX=0 NormalY=0 NormalZ=1 AngleXU=0 Radius=1.75
    g3: Circle CenterX=29 CenterY=14.9 CenterZ=0 NormalX=0 NormalY=0 NormalZ=1 AngleXU=0 Radius=1.75
    g4: Circle CenterX=-27.5 CenterY=-16.6 CenterZ=0 NormalX=0 NormalY=0 NormalZ=1 AngleXU=0 Radius=1.75
    g5: Circle CenterX=27.5 CenterY=-16.6 CenterZ=0 NormalX=0 NormalY=0 NormalZ=1 AngleXU=0 Radius=1.75
  constraints (16):
    c: Symmetric(g0,g0,g-2)
    c: DistanceY(g0,g-1) = 24
    c: DistanceX(g0,g0) = 72
    c: Symmetric(g1,g3,g-2)
    c: Symmetric(g4,g5,g-2)
    c: Equal(g4,g1)
    c: Equal(g1,g2)
    c: Equal(g2,g3)
    c: Equal(g3,g5)
    c: Diameter(g1) = 3.5
    c: DistanceX(g1,g3) = 58
    c: DistanceX(g4,g5) = 55
    c: DistanceY(g5,g3) = 31.5
    c: Horizontal(g1,g2)
    c: PointOnObject(g2,g-2)
    c: DistanceY(g0,g5) = 7.4
FEATURE [Part::Loft] Loft
  Closed = false
  MaxDegree = 5
  Ruled = false
  Sections = -> [Sketch030,Sketch031]
  Solid = true
  TreeRank = 0
FEATURE [Part::Extrusion] Extrude
  Base = -> Sketch012
  Dir = (1,-1e-16,1e-16)
  DirMode = 2
  FaceMakerClass = Part::FaceMakerBullseye
  InnerTaperAngle = 0
  InnerTaperAngleRev = 0
  LengthFwd = 100
  LengthRev = 0
  Solid = true
  Symmetric = true
  TreeRank = 0
FEATURE [Part::MultiCommon] Common
  Shapes = -> [Extrude,Loft]
  TreeRank = 0
FEATURE [Part::FeaturePython] Slice  # WARN: FeaturePython — macro-defined, semantics opaque (R4)
  Base = -> Common
  Mode = 1
  Tolerance = 0
  Tools = -> [Plane002]
  TreeRank = 0
FEATURE [Part::FeaturePython] Slice_child0  label="Slice.Case"  # WARN: FeaturePython — macro-defined, semantics opaque (R4)
  Base = -> Slice
  FilterType = 1
  Invert = false
  OverrideMaxVal = 0
  TreeRank = 0
  WindowFrom = 80
  WindowTo = 100
  items = 0
FEATURE [Part::FeaturePython] Slice_child1  label="Slice.Back"  # WARN: FeaturePython — macro-defined, semantics opaque (R4)
  Base = -> Slice
  FilterType = 1
  Invert = false
  OverrideMaxVal = 0
  TreeRank = 0
  WindowFrom = 80
  WindowTo = 100
  items = 1
FEATURE [App::DocumentObjectGroup] GrExplode_Slice  label="Exploded Slice"
  ClaimAllChildren = true
  ExportMode = 1
  Group = -> [Slice_child0,Slice_child1]
  TreeRank = 0
  _GroupVersion = 1
FEATURE [App::DocumentObjectGroup] Group001  label="BaseShape"
  ClaimAllChildren = true
  ExportMode = 1
  Group = -> [Common,Sketch012,Sketch031,Sketch030,Plane002,GrExplode_Slice]
  TreeRank = 0
  _GroupVersion = 1
FEATURE [PartDesign::FeatureBase] BaseFeature  label="Back.BaseFeature"
  BaseFeature = -> Slice_child1
  NewSolid = false
  Suppress = false
  TreeRank = 0
FEATURE [PartDesign::Pocket] Pocket  label="Back.Pocket.Screws"
  BaseFeature = -> BaseFeature
  ClaimChildren = false
  Fit = 0
  FitJoin = 0
  InnerFit = 0
  InnerFitJoin = 0
  InnerTaperAngle = 0
  InnerTaperAngleRev = 0
  Length = 5
  Length2 = 100
  Midplane = true
  NewSolid = false
  Profile = -> Sketch032
  Suppress = false
  TreeRank = 0
  Type = 1
  _ProfileBasedVersion = 0
FEATURE [PartDesign::FeatureBase] BaseFeature001  label="Case.BaseFeature"
  BaseFeature = -> Slice_child0
  NewSolid = false
  Suppress = false
  TreeRank = 0
FEATURE [PartDesign::Pocket] Pocket001  label="Case.Pocket.Batt"
  BaseFeature = -> BaseFeature001
  ClaimChildren = false
  Fit = 0
  FitJoin = 0
  InnerFit = 0
  InnerFitJoin = 0
  InnerTaperAngle = 0
  InnerTaperAngleRev = 0
  Length = 14.6
  Length2 = 100
  NewSolid = false
  Profile = -> Sketch018
  Reversed = true
  Suppress = false
  TreeRank = 0
  Type = 0
  _ProfileBasedVersion = 0
  expr: Length = <<param>>.batt_carveout
FEATURE [PartDesign::Pad] Pad  label="Case.Pad.Batt"
  BaseFeature = -> Pocket001
  ClaimChildren = false
  Direction = (1,1,1)
  Fit = 0
  FitJoin = 0
  InnerFit = 0
  InnerFitJoin = 0
  InnerTaperAngle = 0
  InnerTaperAngleRev = 0
  Length = 45
  Length2 = 100
  NewSolid = false
  Profile = -> Sketch019
  Suppress = false
  TreeRank = 0
  Type = 0
  _ProfileBasedVersion = 0
  expr: Length = <<param>>.batt_rail_length
FEATURE [PartDesign::Pocket] Pocket002  label="Case.Pocket.Support"
  BaseFeature = -> Pad
  ClaimChildren = false
  Fit = 0
  FitJoin = 0
  InnerFit = 0
  InnerFitJoin = 0
  InnerTaperAngle = 0
  InnerTaperAngleRev = 0
  Length = 5
  Length2 = 100
  NewSolid = false
  Profile = -> Sketch
  Suppress = false
  TreeRank = 0
  Type = 0
  _ProfileBasedVersion = 0
FEATURE [PartDesign::Pocket] Pocket006  label="Case.Pocket.Terminal"
  BaseFeature = -> Pocket002
  ClaimChildren = false
  Fit = 0
  FitJoin = 0
  InnerFit = 0
  InnerFitJoin = 0
  InnerTaperAngle = 0
  InnerTaperAngleRev = 0
  Length = 18.5
  Length2 = 100
  NewSolid = false
  Profile = -> Sketch028
  Suppress = false
  TreeRank = 0
  Type = 0
  _ProfileBasedVersion = 0
  expr: Length = <<param>>.mid_depth / 2 - <<param>>.terminal_depth
FEATURE [PartDesign::Pocket] Pocket005  label="Case.Pocket.Access"
  BaseFeature = -> Pocket006
  ClaimChildren = false
  Fit = 0
  FitJoin = 0
  InnerFit = 0
  InnerFitJoin = 0
  InnerTaperAngle = 0
  InnerTaperAngleRev = 0
  Length = 22.5
  Length2 = 100
  NewSolid = false
  Profile = -> Sketch029
  Reversed = true
  Suppress = false
  TreeRank = 0
  Type = 0
  _ProfileBasedVersion = 0
  expr: Length = <<param>>.terminal_depth
FEATURE [Sketcher::SketchObject] Sketch033  label="SketchFace"
  ArcFitTolerance = 0
  AttachmentSupport = -> [XZ_Plane007]
  FullyConstrained = true
  MapMode = 5
  Placement = pos=(0,0,0) rot=(1,0,0;1.5708rad)
  Support = -> [XZ_Plane007]
  TreeRank = 0
  expr: Constraints[12] = <<param>>.face_radius
  expr: Constraints[21] = <<param>>.face_width1 - 0.4
  expr: Constraints[22] = <<param>>.face_width2 - 0.4
  expr: Constraints[23] = <<param>>.face_height - 0.4
  expr: Constraints[27] = <<param>>.screw_hole + 1
  expr: Constraints[28] = <<param>>.front_screw_width2 / 2
  expr: Constraints[29] = <<param>>.front_screw_width2 / 2
  expr: Constraints[30] = <<param>>.front_screw_width1 / 2
  expr: Constraints[31] = <<param>>.front_screw_width1 / 2
  expr: Constraints[32] = <<param>>.front_screw_height
  expr: Constraints[35] = <<param>>.front_screw_offset + <<param>>.face_offset
  expr: Constraints[48] = <<param>>.face_offset
  sketch-geometry (23):
    g0: LineSegment StartX=-34.3037 StartY=43.4 StartZ=0 EndX=34.3037 EndY=43.4 EndZ=0
    g1: LineSegment StartX=42.3 StartY=35.6438 StartZ=0 EndX=43.05 EndY=11.0438 EndZ=0
    g2: LineSegment StartX=35.0537 StartY=2.8 StartZ=0 EndX=-35.0537 EndY=2.8 EndZ=0
    g3: LineSegment StartX=-43.05 StartY=11.0438 StartZ=0 EndX=-42.3 EndY=35.6438 EndZ=0
    g4: ArcOfCircle CenterX=34.3037 CenterY=35.4 CenterZ=0 NormalX=0 NormalY=0 NormalZ=1 AngleXU=0 Radius=8 StartAngle=0.0304753 EndAngle=1.5708
    g5: ArcOfCircle CenterX=35.0537 CenterY=10.8 CenterZ=0 NormalX=0 NormalY=0 NormalZ=1 AngleXU=0 Radius=8 StartAngle=4.71239 EndAngle=6.31366
    g6: ArcOfCircle CenterX=-34.3037 CenterY=35.4 CenterZ=0 NormalX=0 NormalY=0 NormalZ=1 AngleXU=0 Radius=8 StartAngle=1.5708 EndAngle=3.11112
    g7: ArcOfCircle CenterX=-35.0537 CenterY=10.8 CenterZ=0 NormalX=0 NormalY=0 NormalZ=1 AngleXU=0 Radius=8 StartAngle=3.11111 EndAngle=4.71239
    g8: Circle CenterX=-36.75 CenterY=38.3 CenterZ=0 NormalX=0 NormalY=0 NormalZ=1 AngleXU=0 Radius=1.75
    g9: Circle CenterX=36.75 CenterY=38.3 CenterZ=0 NormalX=0 NormalY=0 NormalZ=1 AngleXU=0 Radius=1.75
    g10: Circle CenterX=-38 CenterY=8.3 CenterZ=0 NormalX=0 NormalY=0 NormalZ=1 AngleXU=0 Radius=1.75
    g11: Circle CenterX=38 CenterY=8.3 CenterZ=0 NormalX=0 NormalY=0 NormalZ=1 AngleXU=0 Radius=1.75
    g12: LineSegment StartX=-14 StartY=33.75 StartZ=0 EndX=14 EndY=33.75 EndZ=0
    g13: LineSegment StartX=16 StartY=31.75 StartZ=0 EndX=16 EndY=19.25 EndZ=0
    g14: LineSegment StartX=14 StartY=17.25 StartZ=0 EndX=-14 EndY=17.25 EndZ=0
    g15: LineSegment StartX=-16 StartY=19.25 StartZ=0 EndX=-16 EndY=31.75 EndZ=0
    g16: ArcOfCircle CenterX=-14 CenterY=31.75 CenterZ=0 NormalX=0 NormalY=0 NormalZ=1 AngleXU=0 Radius=2 StartAngle=1.5708 EndAngle=3.14159
    g17: ArcOfCircle CenterX=-14 CenterY=19.25 CenterZ=0 NormalX=0 NormalY=0 NormalZ=1 AngleXU=0 Radius=2 StartAngle=3.14159 EndAngle=4.71239
    g18: ArcOfCircle CenterX=14 CenterY=19.25 CenterZ=0 NormalX=0 NormalY=0 NormalZ=1 AngleXU=0 Radius=2 StartAngle=4.71239 EndAngle=6.28319
    g19: ArcOfCircle CenterX=14 CenterY=31.75 CenterZ=0 NormalX=0 NormalY=0 NormalZ=1 AngleXU=0 Radius=2 StartAngle=7e-16 EndAngle=1.5708
    g20: Circle CenterX=-31 CenterY=21.5 CenterZ=0 NormalX=0 NormalY=0 NormalZ=1 AngleXU=0 Radius=7.75
    g21: Circle CenterX=31 CenterY=25.5 CenterZ=0 NormalX=0 NormalY=0 NormalZ=1 AngleXU=0 Radius=3.6
    g22: LineSegment [constr] StartX=-69 StartY=25.5 StartZ=0 EndX=31 EndY=25.5 EndZ=0
  constraints (67):
    c: Coincident(g4,g0)
    c: Coincident(g4,g1)
    c: Coincident(g5,g1)
    c: Coincident(g5,g2)
    c: Coincident(g6,g0)
    c: Coincident(g6,g3)
    c: Coincident(g7,g3)
    c: Coincident(g7,g2)
    c: Equal(g1,g3)
    c: Equal(g4,g6)
    c: Equal(g6,g7)
    c: Equal(g7,g5)
    c: Radius(g4) = 8
    c: Tangent(g6,g3)
    c: Tangent(g7,g3)
    c: Tangent(g7,g2)
    c: Tangent(g6,g0)
    c: Tangent(g4,g0)
    c: Tangent(g4,g1)
    c: Tangent(g5,g1)
    c: Tangent(g5,g2)
    c: DistanceX(g3,g1) = 84.6
    c: DistanceX(g3,g1) = 86.1
    c: DistanceY(g2,g0) = 40.6
    c: Equal(g9,g8)
    c: Equal(g8,g10)
    c: Equal(g10,g11)
    c: Diameter(g8) = 3.5
    c: DistanceX(g10,g-1) = 38
    c: DistanceX(g-1,g11) = 38
    c: DistanceX(g-1,g9) = 36.75
    c: DistanceX(g8,g-1) = 36.75
    c: DistanceY(g11,g9) = 30
    c: Horizontal(g8,g9)
    c: Horizontal(g10,g11)
    c: DistanceY(g-1,g11) = 8.3
    c: Horizontal(g12)
    c: Horizontal(g14)
    c: Vertical(g13)
    c: Vertical(g15)
    c: Tangent(g15,g16) = 1.5708
    c: Tangent(g12,g16) = 1.5708
    c: Tangent(g15,g17) = 1.5708
    c: Tangent(g14,g17) = 1.5708
    c: Tangent(g14,g18) = 1.5708
    c: Tangent(g13,g18) = 1.5708
    c: Tangent(g12,g19) = 1.5708
    c: Tangent(g13,g19) = 1.5708
    c: DistanceY(g-1,g2) = 2.8
    c: Horizontal(g0)
    c: Symmetric(g2,g2,g-2)
    c: Diameter(g20) = 15.5
    c: Diameter(g21) = 7.2
    c: Equal(g16,g17)
    c: Equal(g17,g18)
    c: Equal(g18,g19)
    c: DistanceY(g14,g12) = 16.5
    c: DistanceX(g15,g13) = 32
    c: Radius(g19) = 2
    c: DistanceX(g20,g21) = 62
    c: DistanceX(g13,g21) = 15
    c: Symmetric(g12,g14,g22)
    c: DistanceY(g20,g22) = 4
    c: DistanceY(g-1,g22) = 25.5
    c: DistanceX(g-1,g21) = 31
    c: DistanceX(g22,g22) = 100
    c: Coincident(g22,g21)
FEATURE [PartDesign::Pad] Pad001  label="Face.Pad.Face"
  ClaimChildren = false
  Direction = (1,1,1)
  Fit = 0
  FitJoin = 0
  InnerFit = 0
  InnerFitJoin = 0
  InnerTaperAngle = 0
  InnerTaperAngleRev = 0
  Length = 3
  Length2 = 100
  NewSolid = false
  Placement = pos=(0,0,0) rot=(1,0,0;1.5708rad)
  Profile = -> Sketch033
  Suppress = false
  TreeRank = 0
  Type = 0
  _ProfileBasedVersion = 0
  expr: Length = <<param>>.face_thickness
FEATURE [PartDesign::Chamfer] Chamfer001  label="Face.Chamfer.Screen"
  Angle = 45
  Base = -> Pad001 [Edge34]
  BaseFeature = -> Pad001
  ChamferType = 0
  FlipDirection = false
  NewSolid = false
  Placement = pos=(0,0,0) rot=(1,0,0;1.5708rad)
  Size = 2
  Size2 = 1
  SupportTransform = false
  Suppress = false
  TreeRank = 0
FEATURE [PartDesign::Chamfer] Chamfer002  label="Face.Chamfer.Screws"
  Angle = 45
  Base = -> Chamfer001 [Edge54,Edge56,Edge53,Edge55]
  BaseFeature = -> Chamfer001
  ChamferType = 0
  FlipDirection = false
  NewSolid = false
  Placement = pos=(0,0,0) rot=(1,0,0;1.5708rad)
  Size = 1.4
  Size2 = 1
  SupportTransform = false
  Suppress = false
  TreeRank = 0
FEATURE [Sketcher::SketchObject] Sketch034  label="SketchRing"
  ArcFitTolerance = 0
  AttachmentSupport = -> [XZ_Plane008]
  FullyConstrained = true
  MapMode = 5
  Placement = pos=(0,0,0) rot=(1,0,0;1.5708rad)
  Support = -> [XZ_Plane008]
  TreeRank = 0
  sketch-geometry (6):
    g0: LineSegment StartX=-1 StartY=6.25 StartZ=0 EndX=1 EndY=6.25 EndZ=0
    g1: LineSegment StartX=1 StartY=6.25 StartZ=0 EndX=1 EndY=7.75 EndZ=0
    g2: LineSegment StartX=1 StartY=7.75 StartZ=0 EndX=0.3 EndY=7.75 EndZ=0
    g3: LineSegment StartX=0.3 StartY=7.75 StartZ=0 EndX=0.3 EndY=8.75 EndZ=0
    g4: LineSegment StartX=0.3 StartY=8.75 StartZ=0 EndX=-1 EndY=8.75 EndZ=0
    g5: LineSegment StartX=-1 StartY=8.75 StartZ=0 EndX=-1 EndY=6.25 EndZ=0
  constraints (17):
    c: Coincident(g0,g1)
    c: Vertical(g1)
    c: Coincident(g1,g2)
    c: Horizontal(g2)
    c: Coincident(g2,g3)
    c: Vertical(g3)
    c: Coincident(g3,g4)
    c: Horizontal(g4)
    c: Coincident(g4,g5)
    c: Coincident(g5,g0)
    c: Vertical(g5)
    c: DistanceX(g0,g0) = 2
    c: DistanceY(g3,g3) = 1
    c: DistanceX(g4,g4) = 1.3
    c: Symmetric(g0,g0,g-2)
    c: DistanceY(g-1,g0) = 6.25
    c: DistanceY(g5,g5) = 2.5
FEATURE [PartDesign::Revolution] Revolution001  label="Ring.Revolution"
  Angle = 360
  Axis = (1,0,0)
  Base = (0,0,0)
  ClaimChildren = false
  Fit = 0
  FitJoin = 0
  InnerFit = 0
  InnerFitJoin = 0
  NewSolid = false
  Placement = pos=(0,0,0) rot=(1,0,0;1.5708rad)
  Profile = -> Sketch034
  ReferenceAxis = -> X_Axis008
  Suppress = false
  TreeRank = 0
  _ProfileBasedVersion = 0
FEATURE [PartDesign::Body] Body006  label="BodyRing"
  AutoGroupSolids = false
  ClaimAllChildren = false
  ExportMode = 0
  Group = -> [Sketch034,Revolution001]
  Origin = -> Origin008
  Tip = -> Revolution001
  TreeRank = 0
  _ExportChildren = -> [Revolution001]
  _GroupVersion = 1
FEATURE [Part::Box] Box  label="Cube"
  AttacherType = Attacher::AttachEngine3D
  Height = 18
  Length = 18
  Placement = pos=(-9,-0.25,-9) rot=(0,0,1;0rad)
  TreeRank = 0
  Width = 0.5
FEATURE [Part::FeaturePython] Slice001  # WARN: FeaturePython — macro-defined, semantics opaque (R4)
  Base = -> Body006
  Mode = 1
  Tolerance = 0
  Tools = -> [Box]
  TreeRank = 0
FEATURE [Part::FeaturePython] Slice001_child1  label="Slice001.Ring1"  # WARN: FeaturePython — macro-defined, semantics opaque (R4)
  Base = -> Slice001
  FilterType = 1
  Invert = false
  OverrideMaxVal = 0
  TreeRank = 0
  WindowFrom = 80
  WindowTo = 100
  items = 1
FEATURE [Part::FeaturePython] Slice001_child2  label="Slice001.Ring2"  # WARN: FeaturePython — macro-defined, semantics opaque (R4)
  Base = -> Slice001
  FilterType = 1
  Invert = false
  OverrideMaxVal = 0
  TreeRank = 0
  WindowFrom = 80
  WindowTo = 100
  items = 2
FEATURE [App::DocumentObjectGroup] GrExplode_Slice001  label="Ring.Exploded Slice"
  ClaimAllChildren = true
  ExportMode = 1
  Group = -> [Slice001_child1,Slice001_child2]
  TreeRank = 0
  _GroupVersion = 1
FEATURE [Sketcher::SketchObject] Sketch035
  ArcFitTolerance = 0
  AttachmentOffset = pos=(0,0,1.5) rot=(1,0,0;0rad)
  AttachmentSupport = -> [XZ_Plane007]
  ExternalGeometry = -> [Sketch033]
  FullyConstrained = true
  MapMode = 5
  Placement = pos=(0,-1.5,-3e-16) rot=(1,0,0;1.5708rad)
  Support = -> [XZ_Plane007]
  TreeRank = 0
  expr: AttachmentOffset.Base.z = <<param>>.face_thickness - 1.5
  sketch-geometry (1):
    g0: Circle CenterX=-31 CenterY=21.5 CenterZ=0 NormalX=0 NormalY=0 NormalZ=1 AngleXU=0 Radius=9
  constraints (2):
    c: Coincident(g0,g-3)
    c: Diameter(g0) = 18
FEATURE [PartDesign::Pocket] Pocket008  label="Face.Pocket.Lip"
  BaseFeature = -> Chamfer002
  ClaimChildren = false
  Fit = 0
  FitJoin = 0
  InnerFit = 0
  InnerFitJoin = 0
  InnerTaperAngle = 0
  InnerTaperAngleRev = 0
  Length = 1.5
  Length2 = 100
  NewSolid = false
  Placement = pos=(0,0,0) rot=(1,0,0;1.5708rad)
  Profile = -> Sketch035
  Reversed = true
  Suppress = false
  TreeRank = 0
  Type = 1
  _ProfileBasedVersion = 0
FEATURE [Sketcher::SketchObject] Sketch036
  ArcFitTolerance = 0
  AttachmentSupport = -> [XZ_Plane007]
  ExternalGeometry = -> [Sketch033]
  FullyConstrained = true
  MapMode = 5
  Placement = pos=(0,0,0) rot=(1,0,0;1.5708rad)
  Support = -> [XZ_Plane007]
  TreeRank = 0
  sketch-geometry (5):
    g0: ArcOfCircle CenterX=30 CenterY=19.5 CenterZ=0 NormalX=0 NormalY=0 NormalZ=1 AngleXU=0 Radius=0.75 StartAngle=1.5708 EndAngle=4.71239
    g1: ArcOfCircle CenterX=32 CenterY=19.5 CenterZ=0 NormalX=0 NormalY=0 NormalZ=1 AngleXU=0 Radius=0.75 StartAngle=4.71239 EndAngle=7.85398
    g2: LineSegment StartX=30 StartY=18.75 StartZ=0 EndX=32 EndY=18.75 EndZ=0
    g3: LineSegment StartX=30 StartY=20.25 StartZ=0 EndX=32 EndY=20.25 EndZ=0
    g4: LineSegment [constr] StartX=31 StartY=25.5 StartZ=0 EndX=31 EndY=16.5 EndZ=0
  constraints (12):
    c: Tangent(g0,g3) = 1.5708
    c: Tangent(g0,g2) = -1.5708
    c: Tangent(g2,g1) = -1.5708
    c: Tangent(g3,g1) = 1.5708
    c: Horizontal(g2)
    c: Equal(g0,g1)
    c: DistanceY(g1,g-3) = 6
    c: DistanceY(g1,g1) = 1.5
    c: DistanceX(g0,g1) = 2
    c: Coincident(g4,g-3)
    c: Symmetric(g0,g1,g4)
    c: DistanceY(g4,g4) = 9
FEATURE [PartDesign::Pocket] Pocket009  label="Face.Pocket.Notch"
  BaseFeature = -> Pocket008
  ClaimChildren = false
  Fit = 0
  FitJoin = 0
  InnerFit = 0
  InnerFitJoin = 0
  InnerTaperAngle = 0
  InnerTaperAngleRev = 0
  Length = 1
  Length2 = 100
  NewSolid = false
  Placement = pos=(0,0,0) rot=(1,0,0;1.5708rad)
  Profile = -> Sketch036
  Reversed = true
  Suppress = false
  TreeRank = 0
  Type = 0
  _ProfileBasedVersion = 0
FEATURE [PartDesign::Fillet] Fillet  label="Back.Fillet.Big"
  Base = -> Pocket [Edge34,Edge32]
  BaseFeature = -> Pocket
  NewSolid = false
  Radius = 10
  SupportTransform = false
  Suppress = false
  TreeRank = 0
  expr: Radius = <<param>>.radius_big
FEATURE [Sketcher::SketchObject] Sketch037
  ArcFitTolerance = 0
  AttachmentOffset = pos=(0,0,-41) rot=(0,0,1;0rad)
  AttachmentSupport = -> [XZ_Plane005]
  FullyConstrained = true
  MapMode = 5
  Placement = pos=(0,41,9.1e-15) rot=(1,0,0;1.5708rad)
  Support = -> [XZ_Plane005]
  TreeRank = 0
  expr: AttachmentOffset.Base.z = -<<param>>.mid_depth / 2
  expr: Constraints[20] = <<param>>.reart_screw_width2
  expr: Constraints[23] = <<param>>.screw_hole / 2
  expr: Constraints[24] = <<param>>.rear_screw_offset
  expr: Constraints[2] = <<param>>.bottom_height
  sketch-geometry (9):
    g0: Circle [constr] CenterX=0 CenterY=-24 CenterZ=0 NormalX=0 NormalY=0 NormalZ=1 AngleXU=0 Radius=3
    g1: LineSegment StartX=4.5 StartY=-22.8 StartZ=0 EndX=4.5 EndY=-24 EndZ=0
    g2: LineSegment StartX=4.5 StartY=-24 StartZ=0 EndX=11.5 EndY=-24 EndZ=0
    g3: LineSegment StartX=11.5 StartY=-24 StartZ=0 EndX=11.5 EndY=-22.8 EndZ=0
    g4: ArcOfCircle CenterX=5.5 CenterY=-22.8 CenterZ=0 NormalX=0 NormalY=0 NormalZ=1 AngleXU=0 Radius=1 StartAngle=1.5708 EndAngle=3.14159
    g5: ArcOfCircle CenterX=10.5 CenterY=-22.8 CenterZ=0 NormalX=0 NormalY=0 NormalZ=1 AngleXU=0 Radius=1 StartAngle=-9e-16 EndAngle=1.5708
    g6: LineSegment StartX=5.5 StartY=-21.8 StartZ=0 EndX=10.5 EndY=-21.8 EndZ=0
    g7: Circle CenterX=-27.5 CenterY=-16.6 CenterZ=0 NormalX=0 NormalY=0 NormalZ=1 AngleXU=0 Radius=1.25
    g8: Circle CenterX=27.5 CenterY=-16.6 CenterZ=0 NormalX=0 NormalY=0 NormalZ=1 AngleXU=0 Radius=1.25
  constraints (25):
    c: PointOnObject(g0,g-2)
    c: Radius(g0) = 3
    c: DistanceY(g0,g-1) = 24
    c: Vertical(g1)
    c: Coincident(g1,g2)
    c: Horizontal(g2)
    c: Coincident(g2,g3)
    c: Coincident(g5,g3)
    c: Horizontal(g6)
    c: Vertical(g3)
    c: Horizontal(g0,g1)
    c: DistanceX(g0,g1) = 4.5
    c: Equal(g3,g1)
    c: Equal(g4,g5)
    c: Radius(g5) = 1
    c: Tangent(g6,g4) = 1.5708
    c: Tangent(g6,g5) = 1.5708
    c: Tangent(g4,g1) = -1.5708
    c: DistanceY(g2,g5) = 2.2
    c: DistanceX(g1,g2) = 7
    c: DistanceX(g7,g8) = 55
    c: Symmetric(g7,g8,g-2)
    c: Equal(g7,g8)
    c: Radius(g7) = 1.25
    c: DistanceY(g0,g7) = 7.4
FEATURE [PartDesign::Pocket] Pocket010  label="Case.Pocket.Key"
  BaseFeature = -> Pocket005
  ClaimChildren = false
  Fit = 0
  FitJoin = 0
  InnerFit = 0
  InnerFitJoin = 0
  InnerTaperAngle = 0
  InnerTaperAngleRev = 0
  Length = 0
  Length2 = 100
  Midplane = true
  NewSolid = false
  Profile = -> Sketch037
  Suppress = false
  TreeRank = 0
  Type = 3
  UpToFace = -> Pocket005 [Face20]
  _ProfileBasedVersion = 0
FEATURE [PartDesign::SubtractiveLoft] SubtractiveLoft  label="Case.SubtractiveLoft"
  BaseFeature = -> Pocket010
  ClaimChildren = false
  Closed = false
  Fit = 0
  FitJoin = 0
  InnerFit = 0
  InnerFitJoin = 0
  NewSolid = false
  Profile = -> Sketch022
  Ruled = true
  Sections = -> [Sketch025,Sketch023]
  Suppress = false
  TreeRank = 0
  _ProfileBasedVersion = 0
FEATURE [PartDesign::Revolution] Revolution  label="Case.Revolution.Button"
  Angle = 360
  Axis = (-2e-16,0.309017,0.951057)
  Base = (-4.6e-15,10,30.6)
  BaseFeature = -> SubtractiveLoft
  ClaimChildren = false
  Fit = 0
  FitJoin = 0
  InnerFit = 0
  InnerFitJoin = 0
  NewSolid = false
  Profile = -> Sketch021
  ReferenceAxis = -> Sketch021 [V_Axis]
  Reversed = true
  Suppress = false
  TreeRank = 0
  _ProfileBasedVersion = 0
FEATURE [PartDesign::Pocket] Pocket007  label="Case.Pocket.Button"
  BaseFeature = -> Revolution
  ClaimChildren = false
  Fit = 0
  FitJoin = 0
  InnerFit = 0
  InnerFitJoin = 0
  InnerTaperAngle = 0
  InnerTaperAngleRev = 0
  Length = 14
  Length2 = 100
  NewSolid = false
  Profile = -> Sketch008
  Reversed = true
  Suppress = false
  TreeRank = 0
  Type = 0
  _ProfileBasedVersion = 0
FEATURE [PartDesign::Groove] Groove  label="Case.Groove.Button"
  Angle = 360
  Axis = (-2e-16,0.309017,0.951057)
  Base = (-4.1e-15,10,28.6)
  BaseFeature = -> Pocket007
  ClaimChildren = false
  Fit = 0
  FitJoin = 0
  InnerFit = 0
  InnerFitJoin = 0
  NewSolid = false
  Profile = -> Sketch027
  ReferenceAxis = -> Sketch027 [V_Axis]
  Suppress = false
  TreeRank = 0
  _ProfileBasedVersion = 0
FEATURE [PartDesign::Pocket] Pocket004  label="Case.Pocket.Screws"
  BaseFeature = -> Groove
  ClaimChildren = false
  Fit = 0
  FitJoin = 0
  InnerFit = 0
  InnerFitJoin = 0
  InnerTaperAngle = 0
  InnerTaperAngleRev = 0
  Length = 5
  Length2 = 100
  NewSolid = false
  Profile = -> Sketch026
  Suppress = false
  TreeRank = 0
  Type = 0
  _ProfileBasedVersion = 0
FEATURE [PartDesign::Fillet] Fillet008  label="Case.Fillet.Button"
  Base = -> Pocket004 [Edge174]
  BaseFeature = -> Pocket004
  NewSolid = false
  Radius = 10
  SupportTransform = false
  Suppress = false
  TreeRank = 0
FEATURE [PartDesign::Pocket] Pocket003  label="Case.Pocket.Face"
  BaseFeature = -> Fillet008
  ClaimChildren = false
  Fit = 0
  FitJoin = 0
  InnerFit = 0
  InnerFitJoin = 0
  InnerTaperAngle = 0
  InnerTaperAngleRev = 0
  Length = 6
  Length2 = 100
  NewSolid = false
  Profile = -> Sketch024
  Reversed = true
  Suppress = false
  TreeRank = 0
  Type = 0
  _ProfileBasedVersion = 0
  expr: Length = <<param>>.face_thickness * 2
FEATURE [PartDesign::Fillet] Fillet005  label="Case.Fillet.Top"
  Base = -> Pocket003 [Edge2,Edge5]
  BaseFeature = -> Pocket003
  NewSolid = false
  Radius = 10
  SupportTransform = false
  Suppress = false
  TreeRank = 0
  expr: Radius = <<param>>.radius_big
FEATURE [Part::Part2DObjectPython] ShapeString  label="Face.ShapeString"  # Draft 2D object (typed FeaturePython)
  AttachmentOffset = pos=(0,7,1.5) rot=(0,0,1;0rad)
  AttachmentSupport = -> [XZ_Plane007]
  FontFile = <path>
  MapMode = 5
  Placement = pos=(0,-1.5,7) rot=(1,0,0;1.5708rad)
  Size = 5
  String = KSGER
  Support = -> [XZ_Plane007]
  Tracking = 0
  TreeRank = 1
  expr: AttachmentOffset.Base.y = 7
  expr: AttachmentOffset.Base.z = <<param>>.face_thickness / 2
FEATURE [PartDesign::SubShapeBinder] Import  label="Import(ShapeString)"
  BindCopyOnChange = 0
  BindMode = 0
  ClaimChildren = false
  Context = -> Part [Body005.Import.]
  FillStyle = 0
  Fuse = false
  MakeFace = false
  OffsetFill = false
  OffsetIntersection = false
  OffsetJoinType = 0
  OffsetOpenResult = false
  PartialLoad = false
  Relative = true
  Support = -> [ShapeString]
  TreeRank = 2
  _Version = 8
FEATURE [PartDesign::Pocket] Pocket011  label="PocketName"
  BaseFeature = -> Pocket009
  ClaimChildren = false
  Fit = 0
  FitJoin = 0
  InnerFit = 0
  InnerFitJoin = 0
  InnerTaperAngle = 0
  InnerTaperAngleRev = 0
  Length = 10
  Length2 = 100
  Linearize = true
  NewSolid = false
  Placement = pos=(0,0,0) rot=(1,0,0;1.5708rad)
  Profile = -> Import
  Reversed = true
  Suppress = false
  TreeRank = 3
  Type = 0
  _ProfileBasedVersion = 1
FEATURE [PartDesign::Body] Body005  label="BodyFace"
  AutoGroupSolids = false
  ClaimAllChildren = false
  ExportMode = 0
  Group = -> [Sketch033,Pad001,Chamfer001,Chamfer002,Sketch035,Pocket008,Sketch036,Pocket009,Import,ShapeString,Pocket011]
  Origin = -> Origin007
  Placement = pos=(0,-38,0.25) rot=(1,0,0;-0.349066rad)
  Tip = -> Pocket011
  TreeRank = 0
  _ExportChildren = -> [Pad001,Chamfer001,Chamfer002,Pocket008,Pocket009,ShapeString,Pocket011]
  _GroupVersion = 1
  expr: Placement.Base.y = -<<param>>.mid_depth / 2 + <<param>>.face_thickness
  expr: Placement.Rotation.Angle = -<<param>>.front_angle
FEATURE [Mesh::Feature] Mesh006  label="SliceRing (Meshed)"
  TreeRank = 5
FEATURE [Mesh::Feature] Mesh007  label="BodyFace (Meshed)"
  TreeRank = 6
FEATURE [PartDesign::Fillet] Fillet009  label="Back.Fillet.Bottom"
  Base = -> Fillet [Edge32,Edge37]
  BaseFeature = -> Fillet
  NewSolid = false
  Radius = 3
  SupportTransform = false
  Suppress = false
  TreeRank = 7
  expr: Radius = <<param>>.radius_medium
FEATURE [PartDesign::Fillet] Fillet004  label="Back.Fillet.Rear"
  Base = -> Fillet009 [Edge42]
  BaseFeature = -> Fillet009
  NewSolid = false
  Radius = 3
  SupportTransform = false
  Suppress = false
  TreeRank = 0
  expr: Radius = <<param>>.radius_medium
FEATURE [PartDesign::Chamfer] Chamfer  label="Back.Chamfer.Screws"
  Angle = 45
  Base = -> Fillet004 [Edge73,Edge71,Edge69,Edge42,Edge43]
  BaseFeature = -> Fillet004
  ChamferType = 0
  FlipDirection = false
  NewSolid = false
  Size = 1.4
  Size2 = 1
  SupportTransform = false
  Suppress = false
  TreeRank = 0
FEATURE [PartDesign::Body] Body  label="BodyBack"
  AutoGroupSolids = false
  BaseFeature = -> Slice_child1
  ClaimAllChildren = false
  ExportMode = 0
  Group = -> [BaseFeature,Sketch032,Pocket,Fillet,Fillet009,Fillet004,Chamfer]
  Origin = -> Origin
  Tip = -> Chamfer
  TreeRank = 0
  _ExportChildren = -> [BaseFeature,Pocket,Fillet,Fillet009,Fillet004,Chamfer]
  _GroupVersion = 1
FEATURE [PartDesign::Fillet] Fillet010  label="Case.Fillet.Bottom"
  Base = -> Fillet005 [Edge118,Edge99]
  BaseFeature = -> Fillet005
  NewSolid = false
  Radius = 3
  SupportTransform = false
  Suppress = false
  TreeRank = 8
  expr: Radius = <<param>>.radius_medium
FEATURE [PartDesign::Fillet] Fillet011  label="Case.Fillet.Face"
  Base = -> Fillet010 [Edge81]
  BaseFeature = -> Fillet010
  NewSolid = false
  Radius = 2
  SupportTransform = false
  Suppress = false
  TreeRank = 9
  expr: Radius = <<param>>.radius_small
FEATURE [PartDesign::Fillet] Fillet012  label="Case.Fillet.Lower"
  Base = -> Fillet011 [Edge8]
  BaseFeature = -> Fillet011
  NewSolid = false
  Radius = 2
  SupportTransform = false
  Suppress = false
  TreeRank = 10
  expr: Radius = <<param>>.radius_small
FEATURE [PartDesign::Body] Body004  label="BodyCase"
  AutoGroupSolids = false
  BaseFeature = -> Slice_child0
  ClaimAllChildren = false
  ExportMode = 0
  Group = -> [BaseFeature001,Sketch008,Sketch029,Sketch018,Sketch019,Sketch021,Sketch022,Sketch023,Sketch024,Sketch025,Sketch026,Sketch027,Sketch028,Sketch,Pocket001,Pad,Pocket002,Pocket006,Pocket005,Pocket010,SubtractiveLoft,Revolution,Pocket007,Groove,Pocket004,Fillet008,Pocket003,Fillet005,Fillet010,Fillet011,Fillet012,Sketch037]
  Origin = -> Origin005
  Tip = -> Fillet012
  TreeRank = 0
  _ExportChildren = -> [BaseFeature001,Pocket001,Pad,Pocket002,Pocket006,Pocket005,Pocket010,SubtractiveLoft,Revolution,Pocket007,Groove,Pocket004,Fillet008,Pocket003,Fillet005,Fillet010,Fillet011,Fillet012]
  _GroupVersion = 1
FEATURE [Mesh::Feature] Mesh  label="BodyBack (Meshed)"
  TreeRank = 11
FEATURE [Mesh::Feature] Mesh008  label="BodyCase (Meshed)"
  TreeRank = 12
FEATURE [Mesh::Feature] Mesh009  label="BodyFaceKSGER (Meshed)"
  TreeRank = 13
FEATURE [App::DocumentObjectGroup] Group  label="Mesh"
  ClaimAllChildren = true
  ExportMode = 1
  Group = -> [Mesh006,Mesh007,Mesh,Mesh008,Mesh009]
  TreeRank = 0
  _GroupVersion = 1
FEATURE [App::Part] Part
  ClaimAllChildren = false
  ExportMode = 1
  Group = -> [Extrude,Plane002,Common,Sketch012,Loft,Slice_child1,Slice_child0,Slice,GrExplode_Slice,Sketch030,Sketch031,Group001,Spreadsheet,Body,Body004,Body005,Group,Mesh006,Mesh007,Mesh,Mesh008,Mesh009]
  Origin = -> Origin006
  TreeRank = 0
  _ExportChildren = -> [Group001,Spreadsheet,Body,Body004,Body005,Group]
  _GroupVersion = 1
note: 1 file-system path scrubbed to <path> (originals preserved in the JSON sidecar)
